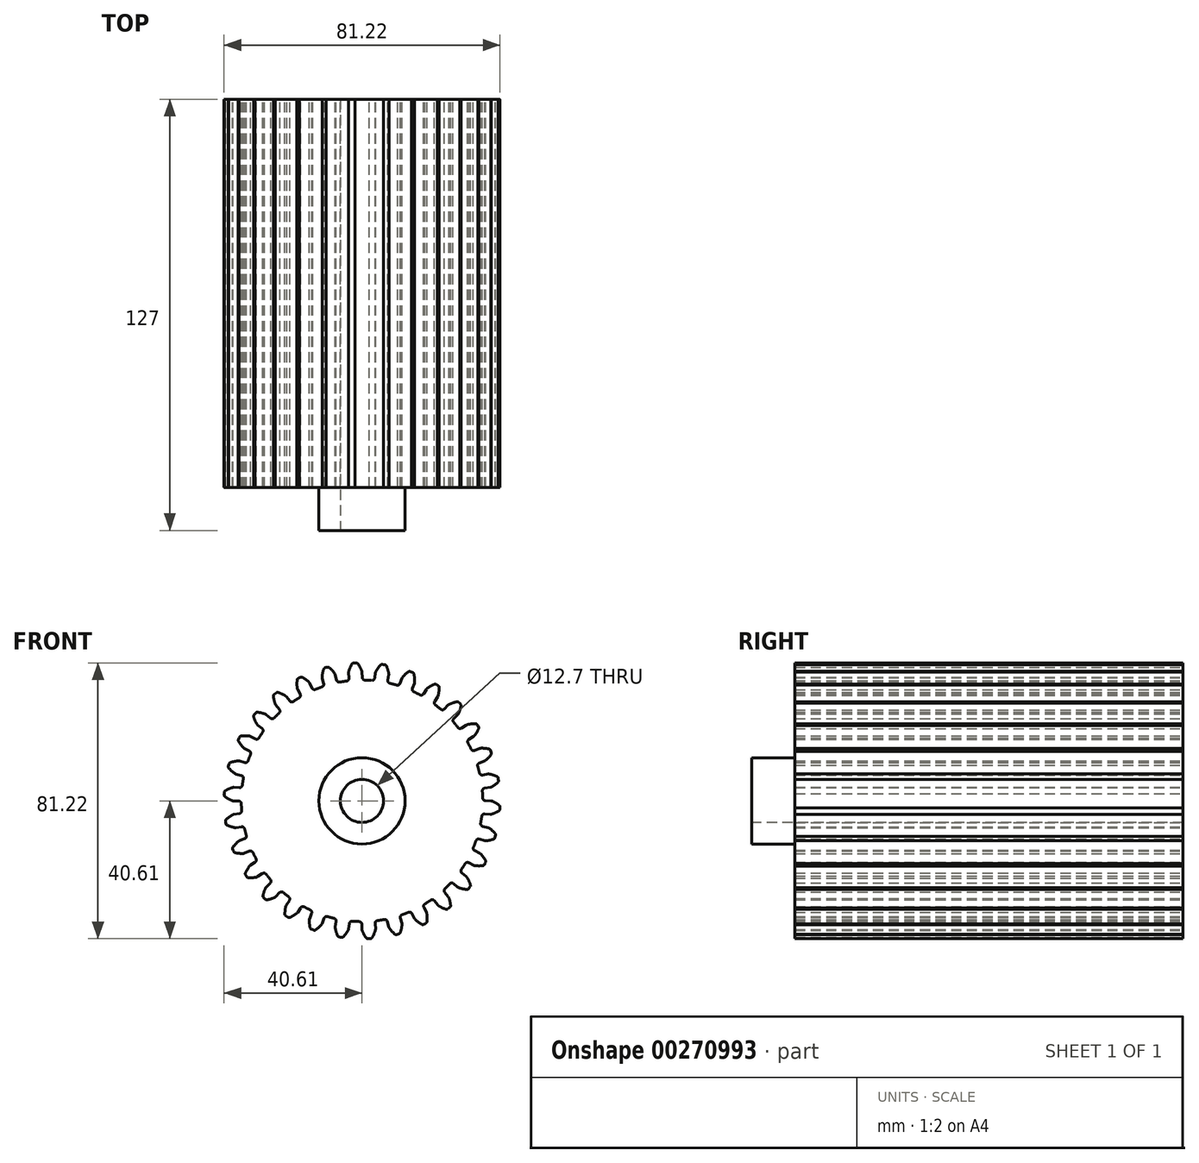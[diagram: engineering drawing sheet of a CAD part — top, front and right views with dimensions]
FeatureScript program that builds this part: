
annotation { "Feature Type Name" : "Feature", "Feature Type Description" : "" }
export const myFeature = defineFeature(function(context is Context, id is Id, definition is map)
    precondition{}
    {
        {
            var Q0;
            Q0=qCreatedBy(makeId("Front.planeOp"),FACE);
            var sketch = newSketch(context, id + "F0", { "sketchPlane" : qUnion([Q0])});
            skArc(sketch, "E0", {"start": v(-4.56, 35.27) * mm, "mid": v(-5.56, 35.12) * mm, "end": v(-6.57, 34.95) * mm});
            skArc(sketch, "E1.trimOffspring", {"start": v(-0.05, 38.23) * mm, "mid": v(-0.6, 39.36) * mm, "end": v(-1.28, 40.4) * mm});
            skLineSegment(sketch, "E2", {"start": v(-1.7, 40.6) * mm, "end": v(-2.13, 40.6) * mm});
            skLineSegment(sketch, "E3", {"start": v(0, 37.97) * mm, "end": v(0.07, 36.31) * mm});
            skLineSegment(sketch, "E4.MirrorCS", {"start": v(-2.55, 40.56) * mm, "end": v(-2.13, 40.6) * mm});
            skArc(sketch, "E5.MirrorCS", {"start": v(-3.95, 38.03) * mm, "mid": v(-3.53, 39.2) * mm, "end": v(-2.95, 40.31) * mm});
            skLineSegment(sketch, "E6.MirrorCS", {"start": v(-3.97, 37.76) * mm, "end": v(-3.86, 36.1) * mm});
            skPoint(sketch, "E7.visualSharp", {"position": v(-2.81, 40.54) * mm});
            skArc(sketch, "E7.filletArc", {"start": v(-2.55, 40.56) * mm, "mid": v(-2.78, 40.49) * mm, "end": v(-2.95, 40.31) * mm});
            skPoint(sketch, "E8.visualSharp", {"position": v(-1.44, 40.61) * mm});
            skArc(sketch, "E8.filletArc", {"start": v(-1.28, 40.4) * mm, "mid": v(-1.46, 40.56) * mm, "end": v(-1.7, 40.6) * mm});
            skPoint(sketch, "E9.visualSharp", {"position": v(-3.82, 35.35) * mm});
            skArc(sketch, "E9.filletArc", {"start": v(-4.56, 35.27) * mm, "mid": v(-4.04, 35.55) * mm, "end": v(-3.86, 36.1) * mm});
            skPoint(sketch, "E10.visualSharp", {"position": v(0.1, 35.56) * mm});
            skArc(sketch, "E10.filletArc", {"start": v(0.07, 36.31) * mm, "mid": v(0.3, 35.78) * mm, "end": v(0.84, 35.55) * mm});
            skPoint(sketch, "E11.visualSharp", {"position": v(0, 38.1) * mm});
            skArc(sketch, "E11.filletArc", {"start": v(0, 37.97) * mm, "mid": v(-0.01, 38.1) * mm, "end": v(-0.05, 38.23) * mm});
            skPoint(sketch, "E12.visualSharp", {"position": v(-3.98, 37.9) * mm});
            skArc(sketch, "E12.filletArc", {"start": v(-3.95, 38.03) * mm, "mid": v(-3.97, 37.9) * mm, "end": v(-3.97, 37.76) * mm});
            skArc(sketch, "E13.1.0", {"start": v(-11.79, 33.55) * mm, "mid": v(-11.35, 33.93) * mm, "end": v(-11.29, 34.51) * mm});
            skLineSegment(sketch, "E13.1.1", {"start": v(-11.74, 36.1) * mm, "end": v(-11.29, 34.51) * mm});
            skArc(sketch, "E13.1.2", {"start": v(-11.77, 36.38) * mm, "mid": v(-11.76, 36.24) * mm, "end": v(-11.74, 36.1) * mm});
            skArc(sketch, "E13.1.3", {"start": v(-11.77, 36.38) * mm, "mid": v(-11.6, 37.61) * mm, "end": v(-11.27, 38.82) * mm});
            skArc(sketch, "E13.1.4", {"start": v(-10.93, 39.14) * mm, "mid": v(-11.14, 39.02) * mm, "end": v(-11.27, 38.82) * mm});
            skLineSegment(sketch, "E13.1.5", {"start": v(-10.1, 39.36) * mm, "end": v(-10.52, 39.26) * mm});
            skArc(sketch, "E13.1.6", {"start": v(-9.65, 39.25) * mm, "mid": v(-9.86, 39.37) * mm, "end": v(-10.1, 39.36) * mm});
            skLineSegment(sketch, "E13.1.7", {"start": v(-10.93, 39.14) * mm, "end": v(-10.52, 39.26) * mm});
            skArc(sketch, "E13.1.8", {"start": v(-8, 37.38) * mm, "mid": v(-8.76, 38.37) * mm, "end": v(-9.65, 39.25) * mm});
            skArc(sketch, "E13.1.9", {"start": v(-7.89, 37.14) * mm, "mid": v(-7.93, 37.27) * mm, "end": v(-8, 37.38) * mm});
            skLineSegment(sketch, "E13.1.10", {"start": v(-7.89, 37.14) * mm, "end": v(-7.48, 35.53) * mm});
            skArc(sketch, "E13.1.11", {"start": v(-7.48, 35.53) * mm, "mid": v(-7.14, 35.06) * mm, "end": v(-6.57, 34.95) * mm});
            skArc(sketch, "E13.2.0", {"start": v(-18.5, 30.37) * mm, "mid": v(-18.15, 30.83) * mm, "end": v(-18.22, 31.41) * mm});
            skLineSegment(sketch, "E13.2.1", {"start": v(-18.99, 32.88) * mm, "end": v(-18.22, 31.41) * mm});
            skArc(sketch, "E13.2.2", {"start": v(-19.07, 33.13) * mm, "mid": v(-19.04, 33) * mm, "end": v(-18.99, 32.88) * mm});
            skArc(sketch, "E13.2.3", {"start": v(-19.07, 33.13) * mm, "mid": v(-19.17, 34.38) * mm, "end": v(-19.1, 35.63) * mm});
            skArc(sketch, "E13.2.4", {"start": v(-18.83, 36.01) * mm, "mid": v(-19.01, 35.85) * mm, "end": v(-19.1, 35.63) * mm});
            skLineSegment(sketch, "E13.2.5", {"start": v(-18.07, 36.4) * mm, "end": v(-18.45, 36.22) * mm});
            skArc(sketch, "E13.2.6", {"start": v(-17.6, 36.4) * mm, "mid": v(-17.83, 36.45) * mm, "end": v(-18.07, 36.4) * mm});
            skLineSegment(sketch, "E13.2.7", {"start": v(-18.83, 36.01) * mm, "end": v(-18.45, 36.22) * mm});
            skArc(sketch, "E13.2.8", {"start": v(-15.6, 34.9) * mm, "mid": v(-16.55, 35.71) * mm, "end": v(-17.6, 36.4) * mm});
            skArc(sketch, "E13.2.9", {"start": v(-15.44, 34.69) * mm, "mid": v(-15.5, 34.8) * mm, "end": v(-15.6, 34.9) * mm});
            skLineSegment(sketch, "E13.2.10", {"start": v(-15.44, 34.69) * mm, "end": v(-14.7, 33.2) * mm});
            skArc(sketch, "E13.2.11", {"start": v(-14.7, 33.2) * mm, "mid": v(-14.27, 32.8) * mm, "end": v(-13.69, 32.82) * mm});
            skArc(sketch, "E13.3.0", {"start": v(-24.41, 25.85) * mm, "mid": v(-24.17, 26.38) * mm, "end": v(-24.35, 26.94) * mm});
            skLineSegment(sketch, "E13.3.1", {"start": v(-25.4, 28.21) * mm, "end": v(-24.35, 26.94) * mm});
            skArc(sketch, "E13.3.2", {"start": v(-25.54, 28.45) * mm, "mid": v(-25.49, 28.32) * mm, "end": v(-25.4, 28.21) * mm});
            skArc(sketch, "E13.3.3", {"start": v(-25.54, 28.45) * mm, "mid": v(-25.9, 29.64) * mm, "end": v(-26.09, 30.88) * mm});
            skArc(sketch, "E13.3.4", {"start": v(-25.9, 31.31) * mm, "mid": v(-26.05, 31.12) * mm, "end": v(-26.09, 30.88) * mm});
            skLineSegment(sketch, "E13.3.5", {"start": v(-25.24, 31.85) * mm, "end": v(-25.58, 31.59) * mm});
            skArc(sketch, "E13.3.6", {"start": v(-24.78, 31.94) * mm, "mid": v(-25.02, 31.95) * mm, "end": v(-25.24, 31.85) * mm});
            skLineSegment(sketch, "E13.3.7", {"start": v(-25.9, 31.31) * mm, "end": v(-25.58, 31.59) * mm});
            skArc(sketch, "E13.3.8", {"start": v(-22.51, 30.9) * mm, "mid": v(-23.61, 31.5) * mm, "end": v(-24.78, 31.94) * mm});
            skArc(sketch, "E13.3.9", {"start": v(-22.31, 30.72) * mm, "mid": v(-22.4, 30.82) * mm, "end": v(-22.51, 30.9) * mm});
            skLineSegment(sketch, "E13.3.10", {"start": v(-22.31, 30.72) * mm, "end": v(-21.29, 29.42) * mm});
            skArc(sketch, "E13.3.11", {"start": v(-21.29, 29.42) * mm, "mid": v(-20.78, 29.12) * mm, "end": v(-20.21, 29.26) * mm});
            skArc(sketch, "E13.4.0", {"start": v(-29.26, 20.21) * mm, "mid": v(-29.12, 20.78) * mm, "end": v(-29.42, 21.29) * mm});
            skLineSegment(sketch, "E13.4.1", {"start": v(-30.72, 22.31) * mm, "end": v(-29.42, 21.29) * mm});
            skArc(sketch, "E13.4.2", {"start": v(-30.9, 22.51) * mm, "mid": v(-30.82, 22.4) * mm, "end": v(-30.72, 22.31) * mm});
            skArc(sketch, "E13.4.3", {"start": v(-30.9, 22.51) * mm, "mid": v(-31.5, 23.61) * mm, "end": v(-31.94, 24.78) * mm});
            skArc(sketch, "E13.4.4", {"start": v(-31.85, 25.24) * mm, "mid": v(-31.95, 25.02) * mm, "end": v(-31.94, 24.78) * mm});
            skLineSegment(sketch, "E13.4.5", {"start": v(-31.31, 25.9) * mm, "end": v(-31.59, 25.58) * mm});
            skArc(sketch, "E13.4.6", {"start": v(-30.88, 26.09) * mm, "mid": v(-31.12, 26.05) * mm, "end": v(-31.31, 25.9) * mm});
            skLineSegment(sketch, "E13.4.7", {"start": v(-31.85, 25.24) * mm, "end": v(-31.59, 25.58) * mm});
            skArc(sketch, "E13.4.8", {"start": v(-28.45, 25.54) * mm, "mid": v(-29.64, 25.9) * mm, "end": v(-30.88, 26.09) * mm});
            skArc(sketch, "E13.4.9", {"start": v(-28.21, 25.4) * mm, "mid": v(-28.32, 25.49) * mm, "end": v(-28.45, 25.54) * mm});
            skLineSegment(sketch, "E13.4.10", {"start": v(-28.21, 25.4) * mm, "end": v(-26.94, 24.35) * mm});
            skArc(sketch, "E13.4.11", {"start": v(-26.94, 24.35) * mm, "mid": v(-26.38, 24.17) * mm, "end": v(-25.85, 24.41) * mm});
            skArc(sketch, "E13.5.0", {"start": v(-32.82, 13.69) * mm, "mid": v(-32.8, 14.27) * mm, "end": v(-33.2, 14.7) * mm});
            skLineSegment(sketch, "E13.5.1", {"start": v(-34.69, 15.44) * mm, "end": v(-33.2, 14.7) * mm});
            skArc(sketch, "E13.5.2", {"start": v(-34.9, 15.6) * mm, "mid": v(-34.8, 15.5) * mm, "end": v(-34.69, 15.44) * mm});
            skArc(sketch, "E13.5.3", {"start": v(-34.9, 15.6) * mm, "mid": v(-35.71, 16.55) * mm, "end": v(-36.4, 17.6) * mm});
            skArc(sketch, "E13.5.4", {"start": v(-36.4, 18.07) * mm, "mid": v(-36.45, 17.83) * mm, "end": v(-36.4, 17.6) * mm});
            skLineSegment(sketch, "E13.5.5", {"start": v(-36.01, 18.83) * mm, "end": v(-36.22, 18.45) * mm});
            skArc(sketch, "E13.5.6", {"start": v(-35.63, 19.1) * mm, "mid": v(-35.85, 19.01) * mm, "end": v(-36.01, 18.83) * mm});
            skLineSegment(sketch, "E13.5.7", {"start": v(-36.4, 18.07) * mm, "end": v(-36.22, 18.45) * mm});
            skArc(sketch, "E13.5.8", {"start": v(-33.13, 19.07) * mm, "mid": v(-34.38, 19.17) * mm, "end": v(-35.63, 19.1) * mm});
            skArc(sketch, "E13.5.9", {"start": v(-32.88, 18.99) * mm, "mid": v(-33, 19.04) * mm, "end": v(-33.13, 19.07) * mm});
            skLineSegment(sketch, "E13.5.10", {"start": v(-32.88, 18.99) * mm, "end": v(-31.41, 18.22) * mm});
            skArc(sketch, "E13.5.11", {"start": v(-31.41, 18.22) * mm, "mid": v(-30.83, 18.15) * mm, "end": v(-30.37, 18.5) * mm});
            skArc(sketch, "E13.6.0", {"start": v(-34.95, 6.57) * mm, "mid": v(-35.06, 7.14) * mm, "end": v(-35.53, 7.48) * mm});
            skLineSegment(sketch, "E13.6.1", {"start": v(-37.14, 7.89) * mm, "end": v(-35.53, 7.48) * mm});
            skArc(sketch, "E13.6.2", {"start": v(-37.38, 8) * mm, "mid": v(-37.27, 7.93) * mm, "end": v(-37.14, 7.89) * mm});
            skArc(sketch, "E13.6.3", {"start": v(-37.38, 8) * mm, "mid": v(-38.37, 8.76) * mm, "end": v(-39.25, 9.65) * mm});
            skArc(sketch, "E13.6.4", {"start": v(-39.36, 10.1) * mm, "mid": v(-39.37, 9.86) * mm, "end": v(-39.25, 9.65) * mm});
            skLineSegment(sketch, "E13.6.5", {"start": v(-39.14, 10.93) * mm, "end": v(-39.26, 10.52) * mm});
            skArc(sketch, "E13.6.6", {"start": v(-38.82, 11.27) * mm, "mid": v(-39.02, 11.14) * mm, "end": v(-39.14, 10.93) * mm});
            skLineSegment(sketch, "E13.6.7", {"start": v(-39.36, 10.1) * mm, "end": v(-39.26, 10.52) * mm});
            skArc(sketch, "E13.6.8", {"start": v(-36.38, 11.77) * mm, "mid": v(-37.61, 11.6) * mm, "end": v(-38.82, 11.27) * mm});
            skArc(sketch, "E13.6.9", {"start": v(-36.1, 11.74) * mm, "mid": v(-36.24, 11.76) * mm, "end": v(-36.38, 11.77) * mm});
            skLineSegment(sketch, "E13.6.10", {"start": v(-36.1, 11.74) * mm, "end": v(-34.51, 11.29) * mm});
            skArc(sketch, "E13.6.11", {"start": v(-34.51, 11.29) * mm, "mid": v(-33.93, 11.35) * mm, "end": v(-33.55, 11.79) * mm});
            skArc(sketch, "E13.7.0", {"start": v(-35.55, -0.84) * mm, "mid": v(-35.78, -0.3) * mm, "end": v(-36.31, -0.07) * mm});
            skLineSegment(sketch, "E13.7.1", {"start": v(-37.97, 0) * mm, "end": v(-36.31, -0.07) * mm});
            skArc(sketch, "E13.7.2", {"start": v(-38.23, 0.05) * mm, "mid": v(-38.1, 0.01) * mm, "end": v(-37.97, 0) * mm});
            skArc(sketch, "E13.7.3", {"start": v(-38.23, 0.05) * mm, "mid": v(-39.36, 0.6) * mm, "end": v(-40.4, 1.28) * mm});
            skArc(sketch, "E13.7.4", {"start": v(-40.6, 1.7) * mm, "mid": v(-40.56, 1.46) * mm, "end": v(-40.4, 1.28) * mm});
            skLineSegment(sketch, "E13.7.5", {"start": v(-40.56, 2.55) * mm, "end": v(-40.6, 2.13) * mm});
            skArc(sketch, "E13.7.6", {"start": v(-40.31, 2.95) * mm, "mid": v(-40.49, 2.78) * mm, "end": v(-40.56, 2.55) * mm});
            skLineSegment(sketch, "E13.7.7", {"start": v(-40.6, 1.7) * mm, "end": v(-40.6, 2.13) * mm});
            skArc(sketch, "E13.7.8", {"start": v(-38.03, 3.95) * mm, "mid": v(-39.2, 3.53) * mm, "end": v(-40.31, 2.95) * mm});
            skArc(sketch, "E13.7.9", {"start": v(-37.76, 3.97) * mm, "mid": v(-37.9, 3.97) * mm, "end": v(-38.03, 3.95) * mm});
            skLineSegment(sketch, "E13.7.10", {"start": v(-37.76, 3.97) * mm, "end": v(-36.1, 3.86) * mm});
            skArc(sketch, "E13.7.11", {"start": v(-36.1, 3.86) * mm, "mid": v(-35.55, 4.04) * mm, "end": v(-35.27, 4.56) * mm});
            skArc(sketch, "E13.8.0", {"start": v(-34.6, -8.22) * mm, "mid": v(-34.93, -7.74) * mm, "end": v(-35.5, -7.62) * mm});
            skLineSegment(sketch, "E13.8.1", {"start": v(-37.13, -7.9) * mm, "end": v(-35.5, -7.62) * mm});
            skArc(sketch, "E13.8.2", {"start": v(-37.4, -7.9) * mm, "mid": v(-37.27, -7.91) * mm, "end": v(-37.13, -7.9) * mm});
            skArc(sketch, "E13.8.3", {"start": v(-37.4, -7.9) * mm, "mid": v(-38.62, -7.6) * mm, "end": v(-39.79, -7.15) * mm});
            skArc(sketch, "E13.8.4", {"start": v(-40.07, -6.78) * mm, "mid": v(-39.97, -7) * mm, "end": v(-39.79, -7.15) * mm});
            skLineSegment(sketch, "E13.8.5", {"start": v(-40.2, -5.93) * mm, "end": v(-40.15, -6.36) * mm});
            skArc(sketch, "E13.8.6", {"start": v(-40.05, -5.5) * mm, "mid": v(-40.18, -5.7) * mm, "end": v(-40.2, -5.93) * mm});
            skLineSegment(sketch, "E13.8.7", {"start": v(-40.07, -6.78) * mm, "end": v(-40.15, -6.36) * mm});
            skArc(sketch, "E13.8.8", {"start": v(-38.02, -4.05) * mm, "mid": v(-39.08, -4.7) * mm, "end": v(-40.05, -5.5) * mm});
            skArc(sketch, "E13.8.9", {"start": v(-37.76, -3.96) * mm, "mid": v(-37.9, -4) * mm, "end": v(-38.02, -4.05) * mm});
            skLineSegment(sketch, "E13.8.10", {"start": v(-37.76, -3.96) * mm, "end": v(-36.12, -3.73) * mm});
            skArc(sketch, "E13.8.11", {"start": v(-36.12, -3.73) * mm, "mid": v(-35.61, -3.44) * mm, "end": v(-35.44, -2.88) * mm});
            skArc(sketch, "E13.9.0", {"start": v(-32.13, -15.23) * mm, "mid": v(-32.56, -14.83) * mm, "end": v(-33.14, -14.83) * mm});
            skLineSegment(sketch, "E13.9.1", {"start": v(-34.68, -15.45) * mm, "end": v(-33.14, -14.83) * mm});
            skArc(sketch, "E13.9.2", {"start": v(-34.95, -15.5) * mm, "mid": v(-34.81, -15.49) * mm, "end": v(-34.68, -15.45) * mm});
            skArc(sketch, "E13.9.3", {"start": v(-34.95, -15.5) * mm, "mid": v(-36.2, -15.47) * mm, "end": v(-37.43, -15.27) * mm});
            skArc(sketch, "E13.9.4", {"start": v(-37.79, -14.96) * mm, "mid": v(-37.64, -15.16) * mm, "end": v(-37.43, -15.27) * mm});
            skLineSegment(sketch, "E13.9.5", {"start": v(-38.1, -14.16) * mm, "end": v(-37.95, -14.57) * mm});
            skArc(sketch, "E13.9.6", {"start": v(-38.03, -13.7) * mm, "mid": v(-38.12, -13.92) * mm, "end": v(-38.1, -14.16) * mm});
            skLineSegment(sketch, "E13.9.7", {"start": v(-37.79, -14.96) * mm, "end": v(-37.95, -14.57) * mm});
            skArc(sketch, "E13.9.8", {"start": v(-36.34, -11.86) * mm, "mid": v(-37.25, -12.72) * mm, "end": v(-38.03, -13.7) * mm});
            skArc(sketch, "E13.9.9", {"start": v(-36.1, -11.73) * mm, "mid": v(-36.23, -11.78) * mm, "end": v(-36.34, -11.86) * mm});
            skLineSegment(sketch, "E13.9.10", {"start": v(-36.1, -11.73) * mm, "end": v(-34.56, -11.16) * mm});
            skArc(sketch, "E13.9.11", {"start": v(-34.56, -11.16) * mm, "mid": v(-34.12, -10.77) * mm, "end": v(-34.07, -10.18) * mm});
            skArc(sketch, "E13.10.0", {"start": v(-28.26, -21.58) * mm, "mid": v(-28.77, -21.28) * mm, "end": v(-29.34, -21.4) * mm});
            skLineSegment(sketch, "E13.10.1", {"start": v(-30.71, -22.32) * mm, "end": v(-29.34, -21.4) * mm});
            skArc(sketch, "E13.10.2", {"start": v(-30.96, -22.43) * mm, "mid": v(-30.83, -22.39) * mm, "end": v(-30.71, -22.32) * mm});
            skArc(sketch, "E13.10.3", {"start": v(-30.96, -22.43) * mm, "mid": v(-32.19, -22.65) * mm, "end": v(-33.44, -22.72) * mm});
            skArc(sketch, "E13.10.4", {"start": v(-33.85, -22.5) * mm, "mid": v(-33.67, -22.66) * mm, "end": v(-33.44, -22.72) * mm});
            skLineSegment(sketch, "E13.10.5", {"start": v(-34.32, -21.77) * mm, "end": v(-34.09, -22.14) * mm});
            skArc(sketch, "E13.10.6", {"start": v(-34.35, -21.3) * mm, "mid": v(-34.4, -21.54) * mm, "end": v(-34.32, -21.77) * mm});
            skLineSegment(sketch, "E13.10.7", {"start": v(-33.85, -22.5) * mm, "end": v(-34.09, -22.14) * mm});
            skArc(sketch, "E13.10.8", {"start": v(-33.08, -19.16) * mm, "mid": v(-33.79, -20.2) * mm, "end": v(-34.35, -21.3) * mm});
            skArc(sketch, "E13.10.9", {"start": v(-32.88, -18.98) * mm, "mid": v(-33, -19.06) * mm, "end": v(-33.08, -19.16) * mm});
            skLineSegment(sketch, "E13.10.10", {"start": v(-32.88, -18.98) * mm, "end": v(-31.48, -18.1) * mm});
            skArc(sketch, "E13.10.11", {"start": v(-31.48, -18.1) * mm, "mid": v(-31.14, -17.62) * mm, "end": v(-31.2, -17.04) * mm});
            skArc(sketch, "E13.11.0", {"start": v(-23.16, -26.98) * mm, "mid": v(-23.71, -26.8) * mm, "end": v(-24.25, -27.03) * mm});
            skLineSegment(sketch, "E13.11.1", {"start": v(-25.4, -28.22) * mm, "end": v(-24.25, -27.03) * mm});
            skArc(sketch, "E13.11.2", {"start": v(-25.62, -28.38) * mm, "mid": v(-25.5, -28.3) * mm, "end": v(-25.4, -28.22) * mm});
            skArc(sketch, "E13.11.3", {"start": v(-25.62, -28.38) * mm, "mid": v(-26.77, -28.85) * mm, "end": v(-27.98, -29.17) * mm});
            skArc(sketch, "E13.11.4", {"start": v(-28.43, -29.04) * mm, "mid": v(-28.22, -29.16) * mm, "end": v(-27.98, -29.17) * mm});
            skLineSegment(sketch, "E13.11.5", {"start": v(-29.04, -28.43) * mm, "end": v(-28.74, -28.74) * mm});
            skArc(sketch, "E13.11.6", {"start": v(-29.17, -27.98) * mm, "mid": v(-29.16, -28.22) * mm, "end": v(-29.04, -28.43) * mm});
            skLineSegment(sketch, "E13.11.7", {"start": v(-28.43, -29.04) * mm, "end": v(-28.74, -28.74) * mm});
            skArc(sketch, "E13.11.8", {"start": v(-28.38, -25.62) * mm, "mid": v(-28.85, -26.77) * mm, "end": v(-29.17, -27.98) * mm});
            skArc(sketch, "E13.11.9", {"start": v(-28.22, -25.4) * mm, "mid": v(-28.3, -25.5) * mm, "end": v(-28.38, -25.62) * mm});
            skLineSegment(sketch, "E13.11.10", {"start": v(-28.22, -25.4) * mm, "end": v(-27.03, -24.25) * mm});
            skArc(sketch, "E13.11.11", {"start": v(-27.03, -24.25) * mm, "mid": v(-26.8, -23.71) * mm, "end": v(-26.98, -23.16) * mm});
            skArc(sketch, "E13.12.0", {"start": v(-17.04, -31.2) * mm, "mid": v(-17.62, -31.14) * mm, "end": v(-18.1, -31.48) * mm});
            skLineSegment(sketch, "E13.12.1", {"start": v(-18.98, -32.88) * mm, "end": v(-18.1, -31.48) * mm});
            skArc(sketch, "E13.12.2", {"start": v(-19.16, -33.08) * mm, "mid": v(-19.06, -33) * mm, "end": v(-18.98, -32.88) * mm});
            skArc(sketch, "E13.12.3", {"start": v(-19.16, -33.08) * mm, "mid": v(-20.2, -33.79) * mm, "end": v(-21.3, -34.35) * mm});
            skArc(sketch, "E13.12.4", {"start": v(-21.77, -34.32) * mm, "mid": v(-21.54, -34.4) * mm, "end": v(-21.3, -34.35) * mm});
            skLineSegment(sketch, "E13.12.5", {"start": v(-22.5, -33.85) * mm, "end": v(-22.14, -34.09) * mm});
            skArc(sketch, "E13.12.6", {"start": v(-22.72, -33.44) * mm, "mid": v(-22.66, -33.67) * mm, "end": v(-22.5, -33.85) * mm});
            skLineSegment(sketch, "E13.12.7", {"start": v(-21.77, -34.32) * mm, "end": v(-22.14, -34.09) * mm});
            skArc(sketch, "E13.12.8", {"start": v(-22.43, -30.96) * mm, "mid": v(-22.65, -32.19) * mm, "end": v(-22.72, -33.44) * mm});
            skArc(sketch, "E13.12.9", {"start": v(-22.32, -30.71) * mm, "mid": v(-22.39, -30.83) * mm, "end": v(-22.43, -30.96) * mm});
            skLineSegment(sketch, "E13.12.10", {"start": v(-22.32, -30.71) * mm, "end": v(-21.4, -29.34) * mm});
            skArc(sketch, "E13.12.11", {"start": v(-21.4, -29.34) * mm, "mid": v(-21.28, -28.77) * mm, "end": v(-21.58, -28.26) * mm});
            skArc(sketch, "E13.13.0", {"start": v(-10.18, -34.07) * mm, "mid": v(-10.77, -34.12) * mm, "end": v(-11.16, -34.56) * mm});
            skLineSegment(sketch, "E13.13.1", {"start": v(-11.73, -36.1) * mm, "end": v(-11.16, -34.56) * mm});
            skArc(sketch, "E13.13.2", {"start": v(-11.86, -36.34) * mm, "mid": v(-11.78, -36.23) * mm, "end": v(-11.73, -36.1) * mm});
            skArc(sketch, "E13.13.3", {"start": v(-11.86, -36.34) * mm, "mid": v(-12.72, -37.25) * mm, "end": v(-13.7, -38.03) * mm});
            skArc(sketch, "E13.13.4", {"start": v(-14.16, -38.1) * mm, "mid": v(-13.92, -38.12) * mm, "end": v(-13.7, -38.03) * mm});
            skLineSegment(sketch, "E13.13.5", {"start": v(-14.96, -37.79) * mm, "end": v(-14.57, -37.95) * mm});
            skArc(sketch, "E13.13.6", {"start": v(-15.27, -37.43) * mm, "mid": v(-15.16, -37.64) * mm, "end": v(-14.96, -37.79) * mm});
            skLineSegment(sketch, "E13.13.7", {"start": v(-14.16, -38.1) * mm, "end": v(-14.57, -37.95) * mm});
            skArc(sketch, "E13.13.8", {"start": v(-15.5, -34.95) * mm, "mid": v(-15.47, -36.2) * mm, "end": v(-15.27, -37.43) * mm});
            skArc(sketch, "E13.13.9", {"start": v(-15.45, -34.68) * mm, "mid": v(-15.49, -34.81) * mm, "end": v(-15.5, -34.95) * mm});
            skLineSegment(sketch, "E13.13.10", {"start": v(-15.45, -34.68) * mm, "end": v(-14.83, -33.14) * mm});
            skArc(sketch, "E13.13.11", {"start": v(-14.83, -33.14) * mm, "mid": v(-14.83, -32.56) * mm, "end": v(-15.23, -32.13) * mm});
            skArc(sketch, "E13.14.0", {"start": v(-2.88, -35.44) * mm, "mid": v(-3.44, -35.61) * mm, "end": v(-3.73, -36.12) * mm});
            skLineSegment(sketch, "E13.14.1", {"start": v(-3.96, -37.76) * mm, "end": v(-3.73, -36.12) * mm});
            skArc(sketch, "E13.14.2", {"start": v(-4.05, -38.02) * mm, "mid": v(-4, -37.9) * mm, "end": v(-3.96, -37.76) * mm});
            skArc(sketch, "E13.14.3", {"start": v(-4.05, -38.02) * mm, "mid": v(-4.7, -39.08) * mm, "end": v(-5.5, -40.05) * mm});
            skArc(sketch, "E13.14.4", {"start": v(-5.93, -40.2) * mm, "mid": v(-5.7, -40.18) * mm, "end": v(-5.5, -40.05) * mm});
            skLineSegment(sketch, "E13.14.5", {"start": v(-6.78, -40.07) * mm, "end": v(-6.36, -40.15) * mm});
            skArc(sketch, "E13.14.6", {"start": v(-7.15, -39.79) * mm, "mid": v(-7, -39.97) * mm, "end": v(-6.78, -40.07) * mm});
            skLineSegment(sketch, "E13.14.7", {"start": v(-5.93, -40.2) * mm, "end": v(-6.36, -40.15) * mm});
            skArc(sketch, "E13.14.8", {"start": v(-7.9, -37.4) * mm, "mid": v(-7.6, -38.62) * mm, "end": v(-7.15, -39.79) * mm});
            skArc(sketch, "E13.14.9", {"start": v(-7.9, -37.13) * mm, "mid": v(-7.91, -37.27) * mm, "end": v(-7.9, -37.4) * mm});
            skLineSegment(sketch, "E13.14.10", {"start": v(-7.9, -37.13) * mm, "end": v(-7.62, -35.5) * mm});
            skArc(sketch, "E13.14.11", {"start": v(-7.62, -35.5) * mm, "mid": v(-7.74, -34.93) * mm, "end": v(-8.22, -34.6) * mm});
            skArc(sketch, "E13.15.0", {"start": v(4.56, -35.27) * mm, "mid": v(4.04, -35.55) * mm, "end": v(3.86, -36.1) * mm});
            skLineSegment(sketch, "E13.15.1", {"start": v(3.97, -37.76) * mm, "end": v(3.86, -36.1) * mm});
            skArc(sketch, "E13.15.2", {"start": v(3.95, -38.03) * mm, "mid": v(3.97, -37.9) * mm, "end": v(3.97, -37.76) * mm});
            skArc(sketch, "E13.15.3", {"start": v(3.95, -38.03) * mm, "mid": v(3.53, -39.2) * mm, "end": v(2.95, -40.31) * mm});
            skArc(sketch, "E13.15.4", {"start": v(2.55, -40.56) * mm, "mid": v(2.78, -40.49) * mm, "end": v(2.95, -40.31) * mm});
            skLineSegment(sketch, "E13.15.5", {"start": v(1.7, -40.6) * mm, "end": v(2.13, -40.6) * mm});
            skArc(sketch, "E13.15.6", {"start": v(1.28, -40.4) * mm, "mid": v(1.46, -40.56) * mm, "end": v(1.7, -40.6) * mm});
            skLineSegment(sketch, "E13.15.7", {"start": v(2.55, -40.56) * mm, "end": v(2.13, -40.6) * mm});
            skArc(sketch, "E13.15.8", {"start": v(0.05, -38.23) * mm, "mid": v(0.6, -39.36) * mm, "end": v(1.28, -40.4) * mm});
            skArc(sketch, "E13.15.9", {"start": v(0, -37.97) * mm, "mid": v(0.01, -38.1) * mm, "end": v(0.05, -38.23) * mm});
            skLineSegment(sketch, "E13.15.10", {"start": v(0, -37.97) * mm, "end": v(-0.07, -36.31) * mm});
            skArc(sketch, "E13.15.11", {"start": v(-0.07, -36.31) * mm, "mid": v(-0.3, -35.78) * mm, "end": v(-0.84, -35.55) * mm});
            skArc(sketch, "E13.16.0", {"start": v(11.79, -33.55) * mm, "mid": v(11.35, -33.93) * mm, "end": v(11.29, -34.51) * mm});
            skLineSegment(sketch, "E13.16.1", {"start": v(11.74, -36.1) * mm, "end": v(11.29, -34.51) * mm});
            skArc(sketch, "E13.16.2", {"start": v(11.77, -36.38) * mm, "mid": v(11.76, -36.24) * mm, "end": v(11.74, -36.1) * mm});
            skArc(sketch, "E13.16.3", {"start": v(11.77, -36.38) * mm, "mid": v(11.6, -37.61) * mm, "end": v(11.27, -38.82) * mm});
            skArc(sketch, "E13.16.4", {"start": v(10.93, -39.14) * mm, "mid": v(11.14, -39.02) * mm, "end": v(11.27, -38.82) * mm});
            skLineSegment(sketch, "E13.16.5", {"start": v(10.1, -39.36) * mm, "end": v(10.52, -39.26) * mm});
            skArc(sketch, "E13.16.6", {"start": v(9.65, -39.25) * mm, "mid": v(9.86, -39.37) * mm, "end": v(10.1, -39.36) * mm});
            skLineSegment(sketch, "E13.16.7", {"start": v(10.93, -39.14) * mm, "end": v(10.52, -39.26) * mm});
            skArc(sketch, "E13.16.8", {"start": v(8, -37.38) * mm, "mid": v(8.76, -38.37) * mm, "end": v(9.65, -39.25) * mm});
            skArc(sketch, "E13.16.9", {"start": v(7.89, -37.14) * mm, "mid": v(7.93, -37.27) * mm, "end": v(8, -37.38) * mm});
            skLineSegment(sketch, "E13.16.10", {"start": v(7.89, -37.14) * mm, "end": v(7.48, -35.53) * mm});
            skArc(sketch, "E13.16.11", {"start": v(7.48, -35.53) * mm, "mid": v(7.14, -35.06) * mm, "end": v(6.57, -34.95) * mm});
            skArc(sketch, "E13.17.0", {"start": v(18.5, -30.37) * mm, "mid": v(18.15, -30.83) * mm, "end": v(18.22, -31.41) * mm});
            skLineSegment(sketch, "E13.17.1", {"start": v(18.99, -32.88) * mm, "end": v(18.22, -31.41) * mm});
            skArc(sketch, "E13.17.2", {"start": v(19.07, -33.13) * mm, "mid": v(19.04, -33) * mm, "end": v(18.99, -32.88) * mm});
            skArc(sketch, "E13.17.3", {"start": v(19.07, -33.13) * mm, "mid": v(19.17, -34.38) * mm, "end": v(19.1, -35.63) * mm});
            skArc(sketch, "E13.17.4", {"start": v(18.83, -36.01) * mm, "mid": v(19.01, -35.85) * mm, "end": v(19.1, -35.63) * mm});
            skLineSegment(sketch, "E13.17.5", {"start": v(18.07, -36.4) * mm, "end": v(18.45, -36.22) * mm});
            skArc(sketch, "E13.17.6", {"start": v(17.6, -36.4) * mm, "mid": v(17.83, -36.45) * mm, "end": v(18.07, -36.4) * mm});
            skLineSegment(sketch, "E13.17.7", {"start": v(18.83, -36.01) * mm, "end": v(18.45, -36.22) * mm});
            skArc(sketch, "E13.17.8", {"start": v(15.6, -34.9) * mm, "mid": v(16.55, -35.71) * mm, "end": v(17.6, -36.4) * mm});
            skArc(sketch, "E13.17.9", {"start": v(15.44, -34.69) * mm, "mid": v(15.5, -34.8) * mm, "end": v(15.6, -34.9) * mm});
            skLineSegment(sketch, "E13.17.10", {"start": v(15.44, -34.69) * mm, "end": v(14.7, -33.2) * mm});
            skArc(sketch, "E13.17.11", {"start": v(14.7, -33.2) * mm, "mid": v(14.27, -32.8) * mm, "end": v(13.69, -32.82) * mm});
            skArc(sketch, "E13.18.0", {"start": v(24.41, -25.85) * mm, "mid": v(24.17, -26.38) * mm, "end": v(24.35, -26.94) * mm});
            skLineSegment(sketch, "E13.18.1", {"start": v(25.4, -28.21) * mm, "end": v(24.35, -26.94) * mm});
            skArc(sketch, "E13.18.2", {"start": v(25.54, -28.45) * mm, "mid": v(25.49, -28.32) * mm, "end": v(25.4, -28.21) * mm});
            skArc(sketch, "E13.18.3", {"start": v(25.54, -28.45) * mm, "mid": v(25.9, -29.64) * mm, "end": v(26.09, -30.88) * mm});
            skArc(sketch, "E13.18.4", {"start": v(25.9, -31.31) * mm, "mid": v(26.05, -31.12) * mm, "end": v(26.09, -30.88) * mm});
            skLineSegment(sketch, "E13.18.5", {"start": v(25.24, -31.85) * mm, "end": v(25.58, -31.59) * mm});
            skArc(sketch, "E13.18.6", {"start": v(24.78, -31.94) * mm, "mid": v(25.02, -31.95) * mm, "end": v(25.24, -31.85) * mm});
            skLineSegment(sketch, "E13.18.7", {"start": v(25.9, -31.31) * mm, "end": v(25.58, -31.59) * mm});
            skArc(sketch, "E13.18.8", {"start": v(22.51, -30.9) * mm, "mid": v(23.61, -31.5) * mm, "end": v(24.78, -31.94) * mm});
            skArc(sketch, "E13.18.9", {"start": v(22.31, -30.72) * mm, "mid": v(22.4, -30.82) * mm, "end": v(22.51, -30.9) * mm});
            skLineSegment(sketch, "E13.18.10", {"start": v(22.31, -30.72) * mm, "end": v(21.29, -29.42) * mm});
            skArc(sketch, "E13.18.11", {"start": v(21.29, -29.42) * mm, "mid": v(20.78, -29.12) * mm, "end": v(20.21, -29.26) * mm});
            skArc(sketch, "E13.19.0", {"start": v(29.26, -20.21) * mm, "mid": v(29.12, -20.78) * mm, "end": v(29.42, -21.29) * mm});
            skLineSegment(sketch, "E13.19.1", {"start": v(30.72, -22.31) * mm, "end": v(29.42, -21.29) * mm});
            skArc(sketch, "E13.19.2", {"start": v(30.9, -22.51) * mm, "mid": v(30.82, -22.4) * mm, "end": v(30.72, -22.31) * mm});
            skArc(sketch, "E13.19.3", {"start": v(30.9, -22.51) * mm, "mid": v(31.5, -23.61) * mm, "end": v(31.94, -24.78) * mm});
            skArc(sketch, "E13.19.4", {"start": v(31.85, -25.24) * mm, "mid": v(31.95, -25.02) * mm, "end": v(31.94, -24.78) * mm});
            skLineSegment(sketch, "E13.19.5", {"start": v(31.31, -25.9) * mm, "end": v(31.59, -25.58) * mm});
            skArc(sketch, "E13.19.6", {"start": v(30.88, -26.09) * mm, "mid": v(31.12, -26.05) * mm, "end": v(31.31, -25.9) * mm});
            skLineSegment(sketch, "E13.19.7", {"start": v(31.85, -25.24) * mm, "end": v(31.59, -25.58) * mm});
            skArc(sketch, "E13.19.8", {"start": v(28.45, -25.54) * mm, "mid": v(29.64, -25.9) * mm, "end": v(30.88, -26.09) * mm});
            skArc(sketch, "E13.19.9", {"start": v(28.21, -25.4) * mm, "mid": v(28.32, -25.49) * mm, "end": v(28.45, -25.54) * mm});
            skLineSegment(sketch, "E13.19.10", {"start": v(28.21, -25.4) * mm, "end": v(26.94, -24.35) * mm});
            skArc(sketch, "E13.19.11", {"start": v(26.94, -24.35) * mm, "mid": v(26.38, -24.17) * mm, "end": v(25.85, -24.41) * mm});
            skArc(sketch, "E13.20.0", {"start": v(32.82, -13.69) * mm, "mid": v(32.8, -14.27) * mm, "end": v(33.2, -14.7) * mm});
            skLineSegment(sketch, "E13.20.1", {"start": v(34.69, -15.44) * mm, "end": v(33.2, -14.7) * mm});
            skArc(sketch, "E13.20.2", {"start": v(34.9, -15.6) * mm, "mid": v(34.8, -15.5) * mm, "end": v(34.69, -15.44) * mm});
            skArc(sketch, "E13.20.3", {"start": v(34.9, -15.6) * mm, "mid": v(35.71, -16.55) * mm, "end": v(36.4, -17.6) * mm});
            skArc(sketch, "E13.20.4", {"start": v(36.4, -18.07) * mm, "mid": v(36.45, -17.83) * mm, "end": v(36.4, -17.6) * mm});
            skLineSegment(sketch, "E13.20.5", {"start": v(36.01, -18.83) * mm, "end": v(36.22, -18.45) * mm});
            skArc(sketch, "E13.20.6", {"start": v(35.63, -19.1) * mm, "mid": v(35.85, -19.01) * mm, "end": v(36.01, -18.83) * mm});
            skLineSegment(sketch, "E13.20.7", {"start": v(36.4, -18.07) * mm, "end": v(36.22, -18.45) * mm});
            skArc(sketch, "E13.20.8", {"start": v(33.13, -19.07) * mm, "mid": v(34.38, -19.17) * mm, "end": v(35.63, -19.1) * mm});
            skArc(sketch, "E13.20.9", {"start": v(32.88, -18.99) * mm, "mid": v(33, -19.04) * mm, "end": v(33.13, -19.07) * mm});
            skLineSegment(sketch, "E13.20.10", {"start": v(32.88, -18.99) * mm, "end": v(31.41, -18.22) * mm});
            skArc(sketch, "E13.20.11", {"start": v(31.41, -18.22) * mm, "mid": v(30.83, -18.15) * mm, "end": v(30.37, -18.5) * mm});
            skArc(sketch, "E13.21.0", {"start": v(34.95, -6.57) * mm, "mid": v(35.06, -7.14) * mm, "end": v(35.53, -7.48) * mm});
            skLineSegment(sketch, "E13.21.1", {"start": v(37.14, -7.89) * mm, "end": v(35.53, -7.48) * mm});
            skArc(sketch, "E13.21.2", {"start": v(37.38, -8) * mm, "mid": v(37.27, -7.93) * mm, "end": v(37.14, -7.89) * mm});
            skArc(sketch, "E13.21.3", {"start": v(37.38, -8) * mm, "mid": v(38.37, -8.76) * mm, "end": v(39.25, -9.65) * mm});
            skArc(sketch, "E13.21.4", {"start": v(39.36, -10.1) * mm, "mid": v(39.37, -9.86) * mm, "end": v(39.25, -9.65) * mm});
            skLineSegment(sketch, "E13.21.5", {"start": v(39.14, -10.93) * mm, "end": v(39.26, -10.52) * mm});
            skArc(sketch, "E13.21.6", {"start": v(38.82, -11.27) * mm, "mid": v(39.02, -11.14) * mm, "end": v(39.14, -10.93) * mm});
            skLineSegment(sketch, "E13.21.7", {"start": v(39.36, -10.1) * mm, "end": v(39.26, -10.52) * mm});
            skArc(sketch, "E13.21.8", {"start": v(36.38, -11.77) * mm, "mid": v(37.61, -11.6) * mm, "end": v(38.82, -11.27) * mm});
            skArc(sketch, "E13.21.9", {"start": v(36.1, -11.74) * mm, "mid": v(36.24, -11.76) * mm, "end": v(36.38, -11.77) * mm});
            skLineSegment(sketch, "E13.21.10", {"start": v(36.1, -11.74) * mm, "end": v(34.51, -11.29) * mm});
            skArc(sketch, "E13.21.11", {"start": v(34.51, -11.29) * mm, "mid": v(33.93, -11.35) * mm, "end": v(33.55, -11.79) * mm});
            skArc(sketch, "E13.22.0", {"start": v(35.55, 0.84) * mm, "mid": v(35.78, 0.3) * mm, "end": v(36.31, 0.07) * mm});
            skLineSegment(sketch, "E13.22.1", {"start": v(37.97, 0) * mm, "end": v(36.31, 0.07) * mm});
            skArc(sketch, "E13.22.2", {"start": v(38.23, -0.05) * mm, "mid": v(38.1, -0.01) * mm, "end": v(37.97, 0) * mm});
            skArc(sketch, "E13.22.3", {"start": v(38.23, -0.05) * mm, "mid": v(39.36, -0.6) * mm, "end": v(40.4, -1.28) * mm});
            skArc(sketch, "E13.22.4", {"start": v(40.6, -1.7) * mm, "mid": v(40.56, -1.46) * mm, "end": v(40.4, -1.28) * mm});
            skLineSegment(sketch, "E13.22.5", {"start": v(40.56, -2.55) * mm, "end": v(40.6, -2.13) * mm});
            skArc(sketch, "E13.22.6", {"start": v(40.31, -2.95) * mm, "mid": v(40.49, -2.78) * mm, "end": v(40.56, -2.55) * mm});
            skLineSegment(sketch, "E13.22.7", {"start": v(40.6, -1.7) * mm, "end": v(40.6, -2.13) * mm});
            skArc(sketch, "E13.22.8", {"start": v(38.03, -3.95) * mm, "mid": v(39.2, -3.53) * mm, "end": v(40.31, -2.95) * mm});
            skArc(sketch, "E13.22.9", {"start": v(37.76, -3.97) * mm, "mid": v(37.9, -3.97) * mm, "end": v(38.03, -3.95) * mm});
            skLineSegment(sketch, "E13.22.10", {"start": v(37.76, -3.97) * mm, "end": v(36.1, -3.86) * mm});
            skArc(sketch, "E13.22.11", {"start": v(36.1, -3.86) * mm, "mid": v(35.55, -4.04) * mm, "end": v(35.27, -4.56) * mm});
            skArc(sketch, "E13.23.0", {"start": v(34.6, 8.22) * mm, "mid": v(34.93, 7.74) * mm, "end": v(35.5, 7.62) * mm});
            skLineSegment(sketch, "E13.23.1", {"start": v(37.13, 7.9) * mm, "end": v(35.5, 7.62) * mm});
            skArc(sketch, "E13.23.2", {"start": v(37.4, 7.9) * mm, "mid": v(37.27, 7.91) * mm, "end": v(37.13, 7.9) * mm});
            skArc(sketch, "E13.23.3", {"start": v(37.4, 7.9) * mm, "mid": v(38.62, 7.6) * mm, "end": v(39.79, 7.15) * mm});
            skArc(sketch, "E13.23.4", {"start": v(40.07, 6.78) * mm, "mid": v(39.97, 7) * mm, "end": v(39.79, 7.15) * mm});
            skLineSegment(sketch, "E13.23.5", {"start": v(40.2, 5.93) * mm, "end": v(40.15, 6.36) * mm});
            skArc(sketch, "E13.23.6", {"start": v(40.05, 5.5) * mm, "mid": v(40.18, 5.7) * mm, "end": v(40.2, 5.93) * mm});
            skLineSegment(sketch, "E13.23.7", {"start": v(40.07, 6.78) * mm, "end": v(40.15, 6.36) * mm});
            skArc(sketch, "E13.23.8", {"start": v(38.02, 4.05) * mm, "mid": v(39.08, 4.7) * mm, "end": v(40.05, 5.5) * mm});
            skArc(sketch, "E13.23.9", {"start": v(37.76, 3.96) * mm, "mid": v(37.9, 4) * mm, "end": v(38.02, 4.05) * mm});
            skLineSegment(sketch, "E13.23.10", {"start": v(37.76, 3.96) * mm, "end": v(36.12, 3.73) * mm});
            skArc(sketch, "E13.23.11", {"start": v(36.12, 3.73) * mm, "mid": v(35.61, 3.44) * mm, "end": v(35.44, 2.88) * mm});
            skArc(sketch, "E13.24.0", {"start": v(32.13, 15.23) * mm, "mid": v(32.56, 14.83) * mm, "end": v(33.14, 14.83) * mm});
            skLineSegment(sketch, "E13.24.1", {"start": v(34.68, 15.45) * mm, "end": v(33.14, 14.83) * mm});
            skArc(sketch, "E13.24.2", {"start": v(34.95, 15.5) * mm, "mid": v(34.81, 15.49) * mm, "end": v(34.68, 15.45) * mm});
            skArc(sketch, "E13.24.3", {"start": v(34.95, 15.5) * mm, "mid": v(36.2, 15.47) * mm, "end": v(37.43, 15.27) * mm});
            skArc(sketch, "E13.24.4", {"start": v(37.79, 14.96) * mm, "mid": v(37.64, 15.16) * mm, "end": v(37.43, 15.27) * mm});
            skLineSegment(sketch, "E13.24.5", {"start": v(38.1, 14.16) * mm, "end": v(37.95, 14.57) * mm});
            skArc(sketch, "E13.24.6", {"start": v(38.03, 13.7) * mm, "mid": v(38.12, 13.92) * mm, "end": v(38.1, 14.16) * mm});
            skLineSegment(sketch, "E13.24.7", {"start": v(37.79, 14.96) * mm, "end": v(37.95, 14.57) * mm});
            skArc(sketch, "E13.24.8", {"start": v(36.34, 11.86) * mm, "mid": v(37.25, 12.72) * mm, "end": v(38.03, 13.7) * mm});
            skArc(sketch, "E13.24.9", {"start": v(36.1, 11.73) * mm, "mid": v(36.23, 11.78) * mm, "end": v(36.34, 11.86) * mm});
            skLineSegment(sketch, "E13.24.10", {"start": v(36.1, 11.73) * mm, "end": v(34.56, 11.16) * mm});
            skArc(sketch, "E13.24.11", {"start": v(34.56, 11.16) * mm, "mid": v(34.12, 10.77) * mm, "end": v(34.07, 10.18) * mm});
            skArc(sketch, "E13.25.0", {"start": v(28.26, 21.58) * mm, "mid": v(28.77, 21.28) * mm, "end": v(29.34, 21.4) * mm});
            skLineSegment(sketch, "E13.25.1", {"start": v(30.71, 22.32) * mm, "end": v(29.34, 21.4) * mm});
            skArc(sketch, "E13.25.2", {"start": v(30.96, 22.43) * mm, "mid": v(30.83, 22.39) * mm, "end": v(30.71, 22.32) * mm});
            skArc(sketch, "E13.25.3", {"start": v(30.96, 22.43) * mm, "mid": v(32.19, 22.65) * mm, "end": v(33.44, 22.72) * mm});
            skArc(sketch, "E13.25.4", {"start": v(33.85, 22.5) * mm, "mid": v(33.67, 22.66) * mm, "end": v(33.44, 22.72) * mm});
            skLineSegment(sketch, "E13.25.5", {"start": v(34.32, 21.77) * mm, "end": v(34.09, 22.14) * mm});
            skArc(sketch, "E13.25.6", {"start": v(34.35, 21.3) * mm, "mid": v(34.4, 21.54) * mm, "end": v(34.32, 21.77) * mm});
            skLineSegment(sketch, "E13.25.7", {"start": v(33.85, 22.5) * mm, "end": v(34.09, 22.14) * mm});
            skArc(sketch, "E13.25.8", {"start": v(33.08, 19.16) * mm, "mid": v(33.79, 20.2) * mm, "end": v(34.35, 21.3) * mm});
            skArc(sketch, "E13.25.9", {"start": v(32.88, 18.98) * mm, "mid": v(33, 19.06) * mm, "end": v(33.08, 19.16) * mm});
            skLineSegment(sketch, "E13.25.10", {"start": v(32.88, 18.98) * mm, "end": v(31.48, 18.1) * mm});
            skArc(sketch, "E13.25.11", {"start": v(31.48, 18.1) * mm, "mid": v(31.14, 17.62) * mm, "end": v(31.2, 17.04) * mm});
            skArc(sketch, "E13.26.0", {"start": v(23.16, 26.98) * mm, "mid": v(23.71, 26.8) * mm, "end": v(24.25, 27.03) * mm});
            skLineSegment(sketch, "E13.26.1", {"start": v(25.4, 28.22) * mm, "end": v(24.25, 27.03) * mm});
            skArc(sketch, "E13.26.2", {"start": v(25.62, 28.38) * mm, "mid": v(25.5, 28.3) * mm, "end": v(25.4, 28.22) * mm});
            skArc(sketch, "E13.26.3", {"start": v(25.62, 28.38) * mm, "mid": v(26.77, 28.85) * mm, "end": v(27.98, 29.17) * mm});
            skArc(sketch, "E13.26.4", {"start": v(28.43, 29.04) * mm, "mid": v(28.22, 29.16) * mm, "end": v(27.98, 29.17) * mm});
            skLineSegment(sketch, "E13.26.5", {"start": v(29.04, 28.43) * mm, "end": v(28.74, 28.74) * mm});
            skArc(sketch, "E13.26.6", {"start": v(29.17, 27.98) * mm, "mid": v(29.16, 28.22) * mm, "end": v(29.04, 28.43) * mm});
            skLineSegment(sketch, "E13.26.7", {"start": v(28.43, 29.04) * mm, "end": v(28.74, 28.74) * mm});
            skArc(sketch, "E13.26.8", {"start": v(28.38, 25.62) * mm, "mid": v(28.85, 26.77) * mm, "end": v(29.17, 27.98) * mm});
            skArc(sketch, "E13.26.9", {"start": v(28.22, 25.4) * mm, "mid": v(28.3, 25.5) * mm, "end": v(28.38, 25.62) * mm});
            skLineSegment(sketch, "E13.26.10", {"start": v(28.22, 25.4) * mm, "end": v(27.03, 24.25) * mm});
            skArc(sketch, "E13.26.11", {"start": v(27.03, 24.25) * mm, "mid": v(26.8, 23.71) * mm, "end": v(26.98, 23.16) * mm});
            skArc(sketch, "E13.27.0", {"start": v(17.04, 31.2) * mm, "mid": v(17.62, 31.14) * mm, "end": v(18.1, 31.48) * mm});
            skLineSegment(sketch, "E13.27.1", {"start": v(18.98, 32.88) * mm, "end": v(18.1, 31.48) * mm});
            skArc(sketch, "E13.27.2", {"start": v(19.16, 33.08) * mm, "mid": v(19.06, 33) * mm, "end": v(18.98, 32.88) * mm});
            skArc(sketch, "E13.27.3", {"start": v(19.16, 33.08) * mm, "mid": v(20.2, 33.79) * mm, "end": v(21.3, 34.35) * mm});
            skArc(sketch, "E13.27.4", {"start": v(21.77, 34.32) * mm, "mid": v(21.54, 34.4) * mm, "end": v(21.3, 34.35) * mm});
            skLineSegment(sketch, "E13.27.5", {"start": v(22.5, 33.85) * mm, "end": v(22.14, 34.09) * mm});
            skArc(sketch, "E13.27.6", {"start": v(22.72, 33.44) * mm, "mid": v(22.66, 33.67) * mm, "end": v(22.5, 33.85) * mm});
            skLineSegment(sketch, "E13.27.7", {"start": v(21.77, 34.32) * mm, "end": v(22.14, 34.09) * mm});
            skArc(sketch, "E13.27.8", {"start": v(22.43, 30.96) * mm, "mid": v(22.65, 32.19) * mm, "end": v(22.72, 33.44) * mm});
            skArc(sketch, "E13.27.9", {"start": v(22.32, 30.71) * mm, "mid": v(22.39, 30.83) * mm, "end": v(22.43, 30.96) * mm});
            skLineSegment(sketch, "E13.27.10", {"start": v(22.32, 30.71) * mm, "end": v(21.4, 29.34) * mm});
            skArc(sketch, "E13.27.11", {"start": v(21.4, 29.34) * mm, "mid": v(21.28, 28.77) * mm, "end": v(21.58, 28.26) * mm});
            skArc(sketch, "E13.28.0", {"start": v(10.18, 34.07) * mm, "mid": v(10.77, 34.12) * mm, "end": v(11.16, 34.56) * mm});
            skLineSegment(sketch, "E13.28.1", {"start": v(11.73, 36.1) * mm, "end": v(11.16, 34.56) * mm});
            skArc(sketch, "E13.28.2", {"start": v(11.86, 36.34) * mm, "mid": v(11.78, 36.23) * mm, "end": v(11.73, 36.1) * mm});
            skArc(sketch, "E13.28.3", {"start": v(11.86, 36.34) * mm, "mid": v(12.72, 37.25) * mm, "end": v(13.7, 38.03) * mm});
            skArc(sketch, "E13.28.4", {"start": v(14.16, 38.1) * mm, "mid": v(13.92, 38.12) * mm, "end": v(13.7, 38.03) * mm});
            skLineSegment(sketch, "E13.28.5", {"start": v(14.96, 37.79) * mm, "end": v(14.57, 37.95) * mm});
            skArc(sketch, "E13.28.6", {"start": v(15.27, 37.43) * mm, "mid": v(15.16, 37.64) * mm, "end": v(14.96, 37.79) * mm});
            skLineSegment(sketch, "E13.28.7", {"start": v(14.16, 38.1) * mm, "end": v(14.57, 37.95) * mm});
            skArc(sketch, "E13.28.8", {"start": v(15.5, 34.95) * mm, "mid": v(15.47, 36.2) * mm, "end": v(15.27, 37.43) * mm});
            skArc(sketch, "E13.28.9", {"start": v(15.45, 34.68) * mm, "mid": v(15.49, 34.81) * mm, "end": v(15.5, 34.95) * mm});
            skLineSegment(sketch, "E13.28.10", {"start": v(15.45, 34.68) * mm, "end": v(14.83, 33.14) * mm});
            skArc(sketch, "E13.28.11", {"start": v(14.83, 33.14) * mm, "mid": v(14.83, 32.56) * mm, "end": v(15.23, 32.13) * mm});
            skArc(sketch, "E13.29.0", {"start": v(2.88, 35.44) * mm, "mid": v(3.44, 35.61) * mm, "end": v(3.73, 36.12) * mm});
            skLineSegment(sketch, "E13.29.1", {"start": v(3.96, 37.76) * mm, "end": v(3.73, 36.12) * mm});
            skArc(sketch, "E13.29.2", {"start": v(4.05, 38.02) * mm, "mid": v(4, 37.9) * mm, "end": v(3.96, 37.76) * mm});
            skArc(sketch, "E13.29.3", {"start": v(4.05, 38.02) * mm, "mid": v(4.7, 39.08) * mm, "end": v(5.5, 40.05) * mm});
            skArc(sketch, "E13.29.4", {"start": v(5.93, 40.2) * mm, "mid": v(5.7, 40.18) * mm, "end": v(5.5, 40.05) * mm});
            skLineSegment(sketch, "E13.29.5", {"start": v(6.78, 40.07) * mm, "end": v(6.36, 40.15) * mm});
            skArc(sketch, "E13.29.6", {"start": v(7.15, 39.79) * mm, "mid": v(7, 39.97) * mm, "end": v(6.78, 40.07) * mm});
            skLineSegment(sketch, "E13.29.7", {"start": v(5.93, 40.2) * mm, "end": v(6.36, 40.15) * mm});
            skArc(sketch, "E13.29.8", {"start": v(7.9, 37.4) * mm, "mid": v(7.6, 38.62) * mm, "end": v(7.15, 39.79) * mm});
            skArc(sketch, "E13.29.9", {"start": v(7.9, 37.13) * mm, "mid": v(7.91, 37.27) * mm, "end": v(7.9, 37.4) * mm});
            skLineSegment(sketch, "E13.29.10", {"start": v(7.9, 37.13) * mm, "end": v(7.62, 35.5) * mm});
            skArc(sketch, "E13.29.11", {"start": v(7.62, 35.5) * mm, "mid": v(7.74, 34.93) * mm, "end": v(8.22, 34.6) * mm});
            skArc(sketch, "E14.trimOffspring", {"start": v(-11.79, 33.55) * mm, "mid": v(-12.74, 33.2) * mm, "end": v(-13.69, 32.82) * mm});
            skArc(sketch, "E15.trimOffspring", {"start": v(2.88, 35.44) * mm, "mid": v(1.86, 35.51) * mm, "end": v(0.84, 35.55) * mm});
            skArc(sketch, "E16.trimOffspring", {"start": v(-18.5, 30.37) * mm, "mid": v(-19.37, 29.82) * mm, "end": v(-20.21, 29.26) * mm});
            skArc(sketch, "E17.trimOffspring", {"start": v(-24.41, 25.85) * mm, "mid": v(-25.14, 25.14) * mm, "end": v(-25.85, 24.41) * mm});
            skArc(sketch, "E18.trimOffspring", {"start": v(-29.26, 20.21) * mm, "mid": v(-29.82, 19.37) * mm, "end": v(-30.37, 18.5) * mm});
            skArc(sketch, "E19.trimOffspring", {"start": v(-32.82, 13.69) * mm, "mid": v(-33.2, 12.74) * mm, "end": v(-33.55, 11.79) * mm});
            skArc(sketch, "E20.trimOffspring", {"start": v(10.18, 34.07) * mm, "mid": v(9.2, 34.35) * mm, "end": v(8.22, 34.6) * mm});
            skArc(sketch, "E21.trimOffspring", {"start": v(17.04, 31.2) * mm, "mid": v(16.14, 31.68) * mm, "end": v(15.23, 32.13) * mm});
            skArc(sketch, "E22.trimOffspring", {"start": v(23.16, 26.98) * mm, "mid": v(22.38, 27.64) * mm, "end": v(21.58, 28.26) * mm});
            skArc(sketch, "E23.trimOffspring", {"start": v(28.26, 21.58) * mm, "mid": v(27.64, 22.38) * mm, "end": v(26.98, 23.16) * mm});
            skArc(sketch, "E24.trimOffspring", {"start": v(32.13, 15.23) * mm, "mid": v(31.68, 16.14) * mm, "end": v(31.2, 17.04) * mm});
            skArc(sketch, "E25.trimOffspring", {"start": v(34.6, 8.22) * mm, "mid": v(34.35, 9.2) * mm, "end": v(34.07, 10.18) * mm});
            skArc(sketch, "E26.trimOffspring", {"start": v(-34.95, 6.57) * mm, "mid": v(-35.12, 5.56) * mm, "end": v(-35.27, 4.56) * mm});
            skArc(sketch, "E27.trimOffspring", {"start": v(35.55, 0.84) * mm, "mid": v(35.51, 1.86) * mm, "end": v(35.44, 2.88) * mm});
            skArc(sketch, "E28.trimOffspring", {"start": v(-35.55, -0.84) * mm, "mid": v(-35.51, -1.86) * mm, "end": v(-35.44, -2.88) * mm});
            skArc(sketch, "E29.trimOffspring", {"start": v(-32.13, -15.23) * mm, "mid": v(-31.68, -16.14) * mm, "end": v(-31.2, -17.04) * mm});
            skArc(sketch, "E30.trimOffspring", {"start": v(32.82, -13.69) * mm, "mid": v(33.2, -12.74) * mm, "end": v(33.55, -11.79) * mm});
            skArc(sketch, "E31.trimOffspring", {"start": v(-34.6, -8.22) * mm, "mid": v(-34.35, -9.2) * mm, "end": v(-34.07, -10.18) * mm});
            skArc(sketch, "E32.trimOffspring", {"start": v(-28.26, -21.58) * mm, "mid": v(-27.64, -22.38) * mm, "end": v(-26.98, -23.16) * mm});
            skArc(sketch, "E33.trimOffspring", {"start": v(-23.16, -26.98) * mm, "mid": v(-22.38, -27.64) * mm, "end": v(-21.58, -28.26) * mm});
            skArc(sketch, "E34.trimOffspring", {"start": v(34.95, -6.57) * mm, "mid": v(35.12, -5.56) * mm, "end": v(35.27, -4.56) * mm});
            skArc(sketch, "E35.trimOffspring", {"start": v(29.26, -20.21) * mm, "mid": v(29.82, -19.37) * mm, "end": v(30.37, -18.5) * mm});
            skArc(sketch, "E36.trimOffspring", {"start": v(24.41, -25.85) * mm, "mid": v(25.14, -25.14) * mm, "end": v(25.85, -24.41) * mm});
            skArc(sketch, "E37.trimOffspring", {"start": v(18.5, -30.37) * mm, "mid": v(19.37, -29.82) * mm, "end": v(20.21, -29.26) * mm});
            skArc(sketch, "E38.trimOffspring", {"start": v(11.79, -33.55) * mm, "mid": v(12.74, -33.2) * mm, "end": v(13.69, -32.82) * mm});
            skArc(sketch, "E39.trimOffspring", {"start": v(4.56, -35.27) * mm, "mid": v(5.56, -35.12) * mm, "end": v(6.57, -34.95) * mm});
            skArc(sketch, "E40.trimOffspring", {"start": v(-2.88, -35.44) * mm, "mid": v(-1.86, -35.51) * mm, "end": v(-0.84, -35.55) * mm});
            skArc(sketch, "E41.trimOffspring", {"start": v(-10.18, -34.07) * mm, "mid": v(-9.2, -34.35) * mm, "end": v(-8.22, -34.6) * mm});
            skArc(sketch, "E42.trimOffspring", {"start": v(-17.04, -31.2) * mm, "mid": v(-16.14, -31.68) * mm, "end": v(-15.23, -32.13) * mm});
            skSolve(sketch);
        }
        {
            var Q0;
            Q0 = qSketchRegion(id + "F0", true);
            extrude(context, id + "F1", {"entities" : qUnion([Q0]), "depth" : 114.3 * mm});
        }
        {
            var Q0;
            Q0=makeQuery(id+"F1.opExtrude","CAP_FACE",FACE,{"disambiguationData":[OSD([sQuery(id+"F0.wireOp",EDGE,"E0"),sQuery(id+"F0.wireOp",EDGE,"E1.trimOffspring"),sQuery(id+"F0.wireOp",EDGE,"E2"),sQuery(id+"F0.wireOp",EDGE,"E3"),sQuery(id+"F0.wireOp",EDGE,"E4.MirrorCS"),sQuery(id+"F0.wireOp",EDGE,"E5.MirrorCS"),sQuery(id+"F0.wireOp",EDGE,"E6.MirrorCS"),sQuery(id+"F0.wireOp",EDGE,"E7.filletArc"),sQuery(id+"F0.wireOp",EDGE,"E8.filletArc"),sQuery(id+"F0.wireOp",EDGE,"E9.filletArc"),sQuery(id+"F0.wireOp",EDGE,"E10.filletArc"),sQuery(id+"F0.wireOp",EDGE,"E11.filletArc"),sQuery(id+"F0.wireOp",EDGE,"E12.filletArc"),sQuery(id+"F0.wireOp",EDGE,"E13.1.0"),sQuery(id+"F0.wireOp",EDGE,"E13.1.1"),sQuery(id+"F0.wireOp",EDGE,"E13.1.2"),sQuery(id+"F0.wireOp",EDGE,"E13.1.3"),sQuery(id+"F0.wireOp",EDGE,"E13.1.4"),sQuery(id+"F0.wireOp",EDGE,"E13.1.5"),sQuery(id+"F0.wireOp",EDGE,"E13.1.6"),sQuery(id+"F0.wireOp",EDGE,"E13.1.7"),sQuery(id+"F0.wireOp",EDGE,"E13.1.8"),sQuery(id+"F0.wireOp",EDGE,"E13.1.9"),sQuery(id+"F0.wireOp",EDGE,"E13.1.10"),sQuery(id+"F0.wireOp",EDGE,"E13.1.11"),sQuery(id+"F0.wireOp",EDGE,"E13.2.0"),sQuery(id+"F0.wireOp",EDGE,"E13.2.1"),sQuery(id+"F0.wireOp",EDGE,"E13.2.2"),sQuery(id+"F0.wireOp",EDGE,"E13.2.3"),sQuery(id+"F0.wireOp",EDGE,"E13.2.4"),sQuery(id+"F0.wireOp",EDGE,"E13.2.5"),sQuery(id+"F0.wireOp",EDGE,"E13.2.6"),sQuery(id+"F0.wireOp",EDGE,"E13.2.7"),sQuery(id+"F0.wireOp",EDGE,"E13.2.8"),sQuery(id+"F0.wireOp",EDGE,"E13.2.9"),sQuery(id+"F0.wireOp",EDGE,"E13.2.10"),sQuery(id+"F0.wireOp",EDGE,"E13.2.11"),sQuery(id+"F0.wireOp",EDGE,"E13.3.0"),sQuery(id+"F0.wireOp",EDGE,"E13.3.1"),sQuery(id+"F0.wireOp",EDGE,"E13.3.2"),sQuery(id+"F0.wireOp",EDGE,"E13.3.3"),sQuery(id+"F0.wireOp",EDGE,"E13.3.4"),sQuery(id+"F0.wireOp",EDGE,"E13.3.5"),sQuery(id+"F0.wireOp",EDGE,"E13.3.6"),sQuery(id+"F0.wireOp",EDGE,"E13.3.7"),sQuery(id+"F0.wireOp",EDGE,"E13.3.8"),sQuery(id+"F0.wireOp",EDGE,"E13.3.9"),sQuery(id+"F0.wireOp",EDGE,"E13.3.10"),sQuery(id+"F0.wireOp",EDGE,"E13.3.11"),sQuery(id+"F0.wireOp",EDGE,"E13.4.0"),sQuery(id+"F0.wireOp",EDGE,"E13.4.1"),sQuery(id+"F0.wireOp",EDGE,"E13.4.2"),sQuery(id+"F0.wireOp",EDGE,"E13.4.3"),sQuery(id+"F0.wireOp",EDGE,"E13.4.4"),sQuery(id+"F0.wireOp",EDGE,"E13.4.5"),sQuery(id+"F0.wireOp",EDGE,"E13.4.6"),sQuery(id+"F0.wireOp",EDGE,"E13.4.7"),sQuery(id+"F0.wireOp",EDGE,"E13.4.8"),sQuery(id+"F0.wireOp",EDGE,"E13.4.9"),sQuery(id+"F0.wireOp",EDGE,"E13.4.10"),sQuery(id+"F0.wireOp",EDGE,"E13.4.11"),sQuery(id+"F0.wireOp",EDGE,"E13.5.0"),sQuery(id+"F0.wireOp",EDGE,"E13.5.1"),sQuery(id+"F0.wireOp",EDGE,"E13.5.2"),sQuery(id+"F0.wireOp",EDGE,"E13.5.3"),sQuery(id+"F0.wireOp",EDGE,"E13.5.4"),sQuery(id+"F0.wireOp",EDGE,"E13.5.5"),sQuery(id+"F0.wireOp",EDGE,"E13.5.6"),sQuery(id+"F0.wireOp",EDGE,"E13.5.7"),sQuery(id+"F0.wireOp",EDGE,"E13.5.8"),sQuery(id+"F0.wireOp",EDGE,"E13.5.9"),sQuery(id+"F0.wireOp",EDGE,"E13.5.10"),sQuery(id+"F0.wireOp",EDGE,"E13.5.11"),sQuery(id+"F0.wireOp",EDGE,"E13.6.0"),sQuery(id+"F0.wireOp",EDGE,"E13.6.1"),sQuery(id+"F0.wireOp",EDGE,"E13.6.2"),sQuery(id+"F0.wireOp",EDGE,"E13.6.3"),sQuery(id+"F0.wireOp",EDGE,"E13.6.4"),sQuery(id+"F0.wireOp",EDGE,"E13.6.5"),sQuery(id+"F0.wireOp",EDGE,"E13.6.6"),sQuery(id+"F0.wireOp",EDGE,"E13.6.7"),sQuery(id+"F0.wireOp",EDGE,"E13.6.8"),sQuery(id+"F0.wireOp",EDGE,"E13.6.9"),sQuery(id+"F0.wireOp",EDGE,"E13.6.10"),sQuery(id+"F0.wireOp",EDGE,"E13.6.11"),sQuery(id+"F0.wireOp",EDGE,"E13.7.0"),sQuery(id+"F0.wireOp",EDGE,"E13.7.1"),sQuery(id+"F0.wireOp",EDGE,"E13.7.2"),sQuery(id+"F0.wireOp",EDGE,"E13.7.3"),sQuery(id+"F0.wireOp",EDGE,"E13.7.4"),sQuery(id+"F0.wireOp",EDGE,"E13.7.5"),sQuery(id+"F0.wireOp",EDGE,"E13.7.6"),sQuery(id+"F0.wireOp",EDGE,"E13.7.7"),sQuery(id+"F0.wireOp",EDGE,"E13.7.8"),sQuery(id+"F0.wireOp",EDGE,"E13.7.9"),sQuery(id+"F0.wireOp",EDGE,"E13.7.10"),sQuery(id+"F0.wireOp",EDGE,"E13.7.11"),sQuery(id+"F0.wireOp",EDGE,"E13.8.0"),sQuery(id+"F0.wireOp",EDGE,"E13.8.1"),sQuery(id+"F0.wireOp",EDGE,"E13.8.2"),sQuery(id+"F0.wireOp",EDGE,"E13.8.3"),sQuery(id+"F0.wireOp",EDGE,"E13.8.4"),sQuery(id+"F0.wireOp",EDGE,"E13.8.5"),sQuery(id+"F0.wireOp",EDGE,"E13.8.6"),sQuery(id+"F0.wireOp",EDGE,"E13.8.7"),sQuery(id+"F0.wireOp",EDGE,"E13.8.8"),sQuery(id+"F0.wireOp",EDGE,"E13.8.9"),sQuery(id+"F0.wireOp",EDGE,"E13.8.10"),sQuery(id+"F0.wireOp",EDGE,"E13.8.11"),sQuery(id+"F0.wireOp",EDGE,"E13.9.0"),sQuery(id+"F0.wireOp",EDGE,"E13.9.1"),sQuery(id+"F0.wireOp",EDGE,"E13.9.2"),sQuery(id+"F0.wireOp",EDGE,"E13.9.3"),sQuery(id+"F0.wireOp",EDGE,"E13.9.4"),sQuery(id+"F0.wireOp",EDGE,"E13.9.5"),sQuery(id+"F0.wireOp",EDGE,"E13.9.6"),sQuery(id+"F0.wireOp",EDGE,"E13.9.7"),sQuery(id+"F0.wireOp",EDGE,"E13.9.8"),sQuery(id+"F0.wireOp",EDGE,"E13.9.9"),sQuery(id+"F0.wireOp",EDGE,"E13.9.10"),sQuery(id+"F0.wireOp",EDGE,"E13.9.11"),sQuery(id+"F0.wireOp",EDGE,"E13.10.0"),sQuery(id+"F0.wireOp",EDGE,"E13.10.1"),sQuery(id+"F0.wireOp",EDGE,"E13.10.2"),sQuery(id+"F0.wireOp",EDGE,"E13.10.3"),sQuery(id+"F0.wireOp",EDGE,"E13.10.4"),sQuery(id+"F0.wireOp",EDGE,"E13.10.5"),sQuery(id+"F0.wireOp",EDGE,"E13.10.6"),sQuery(id+"F0.wireOp",EDGE,"E13.10.7"),sQuery(id+"F0.wireOp",EDGE,"E13.10.8"),sQuery(id+"F0.wireOp",EDGE,"E13.10.9"),sQuery(id+"F0.wireOp",EDGE,"E13.10.10"),sQuery(id+"F0.wireOp",EDGE,"E13.10.11"),sQuery(id+"F0.wireOp",EDGE,"E13.11.0"),sQuery(id+"F0.wireOp",EDGE,"E13.11.1"),sQuery(id+"F0.wireOp",EDGE,"E13.11.2"),sQuery(id+"F0.wireOp",EDGE,"E13.11.3"),sQuery(id+"F0.wireOp",EDGE,"E13.11.4"),sQuery(id+"F0.wireOp",EDGE,"E13.11.5"),sQuery(id+"F0.wireOp",EDGE,"E13.11.6"),sQuery(id+"F0.wireOp",EDGE,"E13.11.7"),sQuery(id+"F0.wireOp",EDGE,"E13.11.8"),sQuery(id+"F0.wireOp",EDGE,"E13.11.9"),sQuery(id+"F0.wireOp",EDGE,"E13.11.10"),sQuery(id+"F0.wireOp",EDGE,"E13.11.11"),sQuery(id+"F0.wireOp",EDGE,"E13.12.0"),sQuery(id+"F0.wireOp",EDGE,"E13.12.1"),sQuery(id+"F0.wireOp",EDGE,"E13.12.2"),sQuery(id+"F0.wireOp",EDGE,"E13.12.3"),sQuery(id+"F0.wireOp",EDGE,"E13.12.4"),sQuery(id+"F0.wireOp",EDGE,"E13.12.5"),sQuery(id+"F0.wireOp",EDGE,"E13.12.6"),sQuery(id+"F0.wireOp",EDGE,"E13.12.7"),sQuery(id+"F0.wireOp",EDGE,"E13.12.8"),sQuery(id+"F0.wireOp",EDGE,"E13.12.9"),sQuery(id+"F0.wireOp",EDGE,"E13.12.10"),sQuery(id+"F0.wireOp",EDGE,"E13.12.11"),sQuery(id+"F0.wireOp",EDGE,"E13.13.0"),sQuery(id+"F0.wireOp",EDGE,"E13.13.1"),sQuery(id+"F0.wireOp",EDGE,"E13.13.2"),sQuery(id+"F0.wireOp",EDGE,"E13.13.3"),sQuery(id+"F0.wireOp",EDGE,"E13.13.4"),sQuery(id+"F0.wireOp",EDGE,"E13.13.5"),sQuery(id+"F0.wireOp",EDGE,"E13.13.6"),sQuery(id+"F0.wireOp",EDGE,"E13.13.7"),sQuery(id+"F0.wireOp",EDGE,"E13.13.8"),sQuery(id+"F0.wireOp",EDGE,"E13.13.9"),sQuery(id+"F0.wireOp",EDGE,"E13.13.10"),sQuery(id+"F0.wireOp",EDGE,"E13.13.11"),sQuery(id+"F0.wireOp",EDGE,"E13.14.0"),sQuery(id+"F0.wireOp",EDGE,"E13.14.1"),sQuery(id+"F0.wireOp",EDGE,"E13.14.2"),sQuery(id+"F0.wireOp",EDGE,"E13.14.3"),sQuery(id+"F0.wireOp",EDGE,"E13.14.4"),sQuery(id+"F0.wireOp",EDGE,"E13.14.5"),sQuery(id+"F0.wireOp",EDGE,"E13.14.6"),sQuery(id+"F0.wireOp",EDGE,"E13.14.7"),sQuery(id+"F0.wireOp",EDGE,"E13.14.8"),sQuery(id+"F0.wireOp",EDGE,"E13.14.9"),sQuery(id+"F0.wireOp",EDGE,"E13.14.10"),sQuery(id+"F0.wireOp",EDGE,"E13.14.11"),sQuery(id+"F0.wireOp",EDGE,"E13.15.0"),sQuery(id+"F0.wireOp",EDGE,"E13.15.1"),sQuery(id+"F0.wireOp",EDGE,"E13.15.2"),sQuery(id+"F0.wireOp",EDGE,"E13.15.3"),sQuery(id+"F0.wireOp",EDGE,"E13.15.4"),sQuery(id+"F0.wireOp",EDGE,"E13.15.5"),sQuery(id+"F0.wireOp",EDGE,"E13.15.6"),sQuery(id+"F0.wireOp",EDGE,"E13.15.7"),sQuery(id+"F0.wireOp",EDGE,"E13.15.8"),sQuery(id+"F0.wireOp",EDGE,"E13.15.9"),sQuery(id+"F0.wireOp",EDGE,"E13.15.10"),sQuery(id+"F0.wireOp",EDGE,"E13.15.11"),sQuery(id+"F0.wireOp",EDGE,"E13.16.0"),sQuery(id+"F0.wireOp",EDGE,"E13.16.1"),sQuery(id+"F0.wireOp",EDGE,"E13.16.2"),sQuery(id+"F0.wireOp",EDGE,"E13.16.3"),sQuery(id+"F0.wireOp",EDGE,"E13.16.4"),sQuery(id+"F0.wireOp",EDGE,"E13.16.5"),sQuery(id+"F0.wireOp",EDGE,"E13.16.6"),sQuery(id+"F0.wireOp",EDGE,"E13.16.7"),sQuery(id+"F0.wireOp",EDGE,"E13.16.8"),sQuery(id+"F0.wireOp",EDGE,"E13.16.9"),sQuery(id+"F0.wireOp",EDGE,"E13.16.10"),sQuery(id+"F0.wireOp",EDGE,"E13.16.11"),sQuery(id+"F0.wireOp",EDGE,"E13.17.0"),sQuery(id+"F0.wireOp",EDGE,"E13.17.1"),sQuery(id+"F0.wireOp",EDGE,"E13.17.2"),sQuery(id+"F0.wireOp",EDGE,"E13.17.3"),sQuery(id+"F0.wireOp",EDGE,"E13.17.4"),sQuery(id+"F0.wireOp",EDGE,"E13.17.5"),sQuery(id+"F0.wireOp",EDGE,"E13.17.6"),sQuery(id+"F0.wireOp",EDGE,"E13.17.7"),sQuery(id+"F0.wireOp",EDGE,"E13.17.8"),sQuery(id+"F0.wireOp",EDGE,"E13.17.9"),sQuery(id+"F0.wireOp",EDGE,"E13.17.10"),sQuery(id+"F0.wireOp",EDGE,"E13.17.11"),sQuery(id+"F0.wireOp",EDGE,"E13.18.0"),sQuery(id+"F0.wireOp",EDGE,"E13.18.1"),sQuery(id+"F0.wireOp",EDGE,"E13.18.2"),sQuery(id+"F0.wireOp",EDGE,"E13.18.3"),sQuery(id+"F0.wireOp",EDGE,"E13.18.4"),sQuery(id+"F0.wireOp",EDGE,"E13.18.5"),sQuery(id+"F0.wireOp",EDGE,"E13.18.6"),sQuery(id+"F0.wireOp",EDGE,"E13.18.7"),sQuery(id+"F0.wireOp",EDGE,"E13.18.8"),sQuery(id+"F0.wireOp",EDGE,"E13.18.9"),sQuery(id+"F0.wireOp",EDGE,"E13.18.10"),sQuery(id+"F0.wireOp",EDGE,"E13.18.11"),sQuery(id+"F0.wireOp",EDGE,"E13.19.0"),sQuery(id+"F0.wireOp",EDGE,"E13.19.1"),sQuery(id+"F0.wireOp",EDGE,"E13.19.2"),sQuery(id+"F0.wireOp",EDGE,"E13.19.3"),sQuery(id+"F0.wireOp",EDGE,"E13.19.4"),sQuery(id+"F0.wireOp",EDGE,"E13.19.5"),sQuery(id+"F0.wireOp",EDGE,"E13.19.6"),sQuery(id+"F0.wireOp",EDGE,"E13.19.7"),sQuery(id+"F0.wireOp",EDGE,"E13.19.8"),sQuery(id+"F0.wireOp",EDGE,"E13.19.9"),sQuery(id+"F0.wireOp",EDGE,"E13.19.10"),sQuery(id+"F0.wireOp",EDGE,"E13.19.11"),sQuery(id+"F0.wireOp",EDGE,"E13.20.0"),sQuery(id+"F0.wireOp",EDGE,"E13.20.1"),sQuery(id+"F0.wireOp",EDGE,"E13.20.2"),sQuery(id+"F0.wireOp",EDGE,"E13.20.3"),sQuery(id+"F0.wireOp",EDGE,"E13.20.4"),sQuery(id+"F0.wireOp",EDGE,"E13.20.5"),sQuery(id+"F0.wireOp",EDGE,"E13.20.6"),sQuery(id+"F0.wireOp",EDGE,"E13.20.7"),sQuery(id+"F0.wireOp",EDGE,"E13.20.8"),sQuery(id+"F0.wireOp",EDGE,"E13.20.9"),sQuery(id+"F0.wireOp",EDGE,"E13.20.10"),sQuery(id+"F0.wireOp",EDGE,"E13.20.11"),sQuery(id+"F0.wireOp",EDGE,"E13.21.0"),sQuery(id+"F0.wireOp",EDGE,"E13.21.1"),sQuery(id+"F0.wireOp",EDGE,"E13.21.2"),sQuery(id+"F0.wireOp",EDGE,"E13.21.3"),sQuery(id+"F0.wireOp",EDGE,"E13.21.4"),sQuery(id+"F0.wireOp",EDGE,"E13.21.5"),sQuery(id+"F0.wireOp",EDGE,"E13.21.6"),sQuery(id+"F0.wireOp",EDGE,"E13.21.7"),sQuery(id+"F0.wireOp",EDGE,"E13.21.8"),sQuery(id+"F0.wireOp",EDGE,"E13.21.9"),sQuery(id+"F0.wireOp",EDGE,"E13.21.10"),sQuery(id+"F0.wireOp",EDGE,"E13.21.11"),sQuery(id+"F0.wireOp",EDGE,"E13.22.0"),sQuery(id+"F0.wireOp",EDGE,"E13.22.1"),sQuery(id+"F0.wireOp",EDGE,"E13.22.2"),sQuery(id+"F0.wireOp",EDGE,"E13.22.3"),sQuery(id+"F0.wireOp",EDGE,"E13.22.4"),sQuery(id+"F0.wireOp",EDGE,"E13.22.5"),sQuery(id+"F0.wireOp",EDGE,"E13.22.6"),sQuery(id+"F0.wireOp",EDGE,"E13.22.7"),sQuery(id+"F0.wireOp",EDGE,"E13.22.8"),sQuery(id+"F0.wireOp",EDGE,"E13.22.9"),sQuery(id+"F0.wireOp",EDGE,"E13.22.10"),sQuery(id+"F0.wireOp",EDGE,"E13.22.11"),sQuery(id+"F0.wireOp",EDGE,"E13.23.0"),sQuery(id+"F0.wireOp",EDGE,"E13.23.1"),sQuery(id+"F0.wireOp",EDGE,"E13.23.2"),sQuery(id+"F0.wireOp",EDGE,"E13.23.3"),sQuery(id+"F0.wireOp",EDGE,"E13.23.4"),sQuery(id+"F0.wireOp",EDGE,"E13.23.5"),sQuery(id+"F0.wireOp",EDGE,"E13.23.6"),sQuery(id+"F0.wireOp",EDGE,"E13.23.7"),sQuery(id+"F0.wireOp",EDGE,"E13.23.8"),sQuery(id+"F0.wireOp",EDGE,"E13.23.9"),sQuery(id+"F0.wireOp",EDGE,"E13.23.10"),sQuery(id+"F0.wireOp",EDGE,"E13.23.11"),sQuery(id+"F0.wireOp",EDGE,"E13.24.0"),sQuery(id+"F0.wireOp",EDGE,"E13.24.1"),sQuery(id+"F0.wireOp",EDGE,"E13.24.2"),sQuery(id+"F0.wireOp",EDGE,"E13.24.3"),sQuery(id+"F0.wireOp",EDGE,"E13.24.4"),sQuery(id+"F0.wireOp",EDGE,"E13.24.5"),sQuery(id+"F0.wireOp",EDGE,"E13.24.6"),sQuery(id+"F0.wireOp",EDGE,"E13.24.7"),sQuery(id+"F0.wireOp",EDGE,"E13.24.8"),sQuery(id+"F0.wireOp",EDGE,"E13.24.9"),sQuery(id+"F0.wireOp",EDGE,"E13.24.10"),sQuery(id+"F0.wireOp",EDGE,"E13.24.11"),sQuery(id+"F0.wireOp",EDGE,"E13.25.0"),sQuery(id+"F0.wireOp",EDGE,"E13.25.1"),sQuery(id+"F0.wireOp",EDGE,"E13.25.2"),sQuery(id+"F0.wireOp",EDGE,"E13.25.3"),sQuery(id+"F0.wireOp",EDGE,"E13.25.4"),sQuery(id+"F0.wireOp",EDGE,"E13.25.5"),sQuery(id+"F0.wireOp",EDGE,"E13.25.6"),sQuery(id+"F0.wireOp",EDGE,"E13.25.7"),sQuery(id+"F0.wireOp",EDGE,"E13.25.8"),sQuery(id+"F0.wireOp",EDGE,"E13.25.9"),sQuery(id+"F0.wireOp",EDGE,"E13.25.10"),sQuery(id+"F0.wireOp",EDGE,"E13.25.11"),sQuery(id+"F0.wireOp",EDGE,"E13.26.0"),sQuery(id+"F0.wireOp",EDGE,"E13.26.1"),sQuery(id+"F0.wireOp",EDGE,"E13.26.2"),sQuery(id+"F0.wireOp",EDGE,"E13.26.3"),sQuery(id+"F0.wireOp",EDGE,"E13.26.4"),sQuery(id+"F0.wireOp",EDGE,"E13.26.5"),sQuery(id+"F0.wireOp",EDGE,"E13.26.6"),sQuery(id+"F0.wireOp",EDGE,"E13.26.7"),sQuery(id+"F0.wireOp",EDGE,"E13.26.8"),sQuery(id+"F0.wireOp",EDGE,"E13.26.9"),sQuery(id+"F0.wireOp",EDGE,"E13.26.10"),sQuery(id+"F0.wireOp",EDGE,"E13.26.11"),sQuery(id+"F0.wireOp",EDGE,"E13.27.0"),sQuery(id+"F0.wireOp",EDGE,"E13.27.1"),sQuery(id+"F0.wireOp",EDGE,"E13.27.2"),sQuery(id+"F0.wireOp",EDGE,"E13.27.3"),sQuery(id+"F0.wireOp",EDGE,"E13.27.4"),sQuery(id+"F0.wireOp",EDGE,"E13.27.5"),sQuery(id+"F0.wireOp",EDGE,"E13.27.6"),sQuery(id+"F0.wireOp",EDGE,"E13.27.7"),sQuery(id+"F0.wireOp",EDGE,"E13.27.8"),sQuery(id+"F0.wireOp",EDGE,"E13.27.9"),sQuery(id+"F0.wireOp",EDGE,"E13.27.10"),sQuery(id+"F0.wireOp",EDGE,"E13.27.11"),sQuery(id+"F0.wireOp",EDGE,"E13.28.0"),sQuery(id+"F0.wireOp",EDGE,"E13.28.1"),sQuery(id+"F0.wireOp",EDGE,"E13.28.2"),sQuery(id+"F0.wireOp",EDGE,"E13.28.3"),sQuery(id+"F0.wireOp",EDGE,"E13.28.4"),sQuery(id+"F0.wireOp",EDGE,"E13.28.5"),sQuery(id+"F0.wireOp",EDGE,"E13.28.6"),sQuery(id+"F0.wireOp",EDGE,"E13.28.7"),sQuery(id+"F0.wireOp",EDGE,"E13.28.8"),sQuery(id+"F0.wireOp",EDGE,"E13.28.9"),sQuery(id+"F0.wireOp",EDGE,"E13.28.10"),sQuery(id+"F0.wireOp",EDGE,"E13.28.11"),sQuery(id+"F0.wireOp",EDGE,"E13.29.0"),sQuery(id+"F0.wireOp",EDGE,"E13.29.1"),sQuery(id+"F0.wireOp",EDGE,"E13.29.2"),sQuery(id+"F0.wireOp",EDGE,"E13.29.3"),sQuery(id+"F0.wireOp",EDGE,"E13.29.4"),sQuery(id+"F0.wireOp",EDGE,"E13.29.5"),sQuery(id+"F0.wireOp",EDGE,"E13.29.6"),sQuery(id+"F0.wireOp",EDGE,"E13.29.7"),sQuery(id+"F0.wireOp",EDGE,"E13.29.8"),sQuery(id+"F0.wireOp",EDGE,"E13.29.9"),sQuery(id+"F0.wireOp",EDGE,"E13.29.10"),sQuery(id+"F0.wireOp",EDGE,"E13.29.11"),sQuery(id+"F0.wireOp",EDGE,"E14.trimOffspring"),sQuery(id+"F0.wireOp",EDGE,"E15.trimOffspring"),sQuery(id+"F0.wireOp",EDGE,"E16.trimOffspring"),sQuery(id+"F0.wireOp",EDGE,"E17.trimOffspring"),sQuery(id+"F0.wireOp",EDGE,"E18.trimOffspring"),sQuery(id+"F0.wireOp",EDGE,"E19.trimOffspring"),sQuery(id+"F0.wireOp",EDGE,"E20.trimOffspring"),sQuery(id+"F0.wireOp",EDGE,"E21.trimOffspring"),sQuery(id+"F0.wireOp",EDGE,"E22.trimOffspring"),sQuery(id+"F0.wireOp",EDGE,"E23.trimOffspring"),sQuery(id+"F0.wireOp",EDGE,"E24.trimOffspring"),sQuery(id+"F0.wireOp",EDGE,"E25.trimOffspring"),sQuery(id+"F0.wireOp",EDGE,"E26.trimOffspring"),sQuery(id+"F0.wireOp",EDGE,"E27.trimOffspring"),sQuery(id+"F0.wireOp",EDGE,"E28.trimOffspring"),sQuery(id+"F0.wireOp",EDGE,"E29.trimOffspring"),sQuery(id+"F0.wireOp",EDGE,"E30.trimOffspring"),sQuery(id+"F0.wireOp",EDGE,"E31.trimOffspring"),sQuery(id+"F0.wireOp",EDGE,"E32.trimOffspring"),sQuery(id+"F0.wireOp",EDGE,"E33.trimOffspring"),sQuery(id+"F0.wireOp",EDGE,"E34.trimOffspring"),sQuery(id+"F0.wireOp",EDGE,"E35.trimOffspring"),sQuery(id+"F0.wireOp",EDGE,"E36.trimOffspring"),sQuery(id+"F0.wireOp",EDGE,"E37.trimOffspring"),sQuery(id+"F0.wireOp",EDGE,"E38.trimOffspring"),sQuery(id+"F0.wireOp",EDGE,"E39.trimOffspring"),sQuery(id+"F0.wireOp",EDGE,"E40.trimOffspring"),sQuery(id+"F0.wireOp",EDGE,"E41.trimOffspring"),sQuery(id+"F0.wireOp",EDGE,"E42.trimOffspring")])],"isStart":false});
            var sketch = newSketch(context, id + "F2", { "sketchPlane" : qUnion([Q0])});
            skCircle(sketch, "E43", {"center": v(0, 0) * mm, "radius": 12.7 * mm});
            skCircle(sketch, "E44", {"center": v(0, 0) * mm, "radius": 6.35 * mm});
            skSolve(sketch);
        }
        {
            var Q0;
            Q0=makeQuery(id+"F2.imprint","IMPRINT",FACE,{"disambiguationData":[TD([[makeQuery(id+"F2.imprint","IMPRINT",EDGE,{"derivedFrom":sQuery(id+"F2.wireOp",EDGE,"E44")}),1.0]])]});
            extrude(context, id + "F3", {"entities" : qUnion([Q0]), "operationType" : NewBodyOperationType.REMOVE, "endBound" : BoundingType.THROUGH_ALL, "oppositeDirection" : true, "depth" : 12.7 * mm});
        }
        {
            var Q0;
            Q0=makeQuery(id+"F1.opExtrude","CAP_FACE",FACE,{"disambiguationData":[OSD([sQuery(id+"F0.wireOp",EDGE,"E0"),sQuery(id+"F0.wireOp",EDGE,"E1.trimOffspring"),sQuery(id+"F0.wireOp",EDGE,"E2"),sQuery(id+"F0.wireOp",EDGE,"E3"),sQuery(id+"F0.wireOp",EDGE,"E4.MirrorCS"),sQuery(id+"F0.wireOp",EDGE,"E5.MirrorCS"),sQuery(id+"F0.wireOp",EDGE,"E6.MirrorCS"),sQuery(id+"F0.wireOp",EDGE,"E7.filletArc"),sQuery(id+"F0.wireOp",EDGE,"E8.filletArc"),sQuery(id+"F0.wireOp",EDGE,"E9.filletArc"),sQuery(id+"F0.wireOp",EDGE,"E10.filletArc"),sQuery(id+"F0.wireOp",EDGE,"E11.filletArc"),sQuery(id+"F0.wireOp",EDGE,"E12.filletArc"),sQuery(id+"F0.wireOp",EDGE,"E13.1.0"),sQuery(id+"F0.wireOp",EDGE,"E13.1.1"),sQuery(id+"F0.wireOp",EDGE,"E13.1.2"),sQuery(id+"F0.wireOp",EDGE,"E13.1.3"),sQuery(id+"F0.wireOp",EDGE,"E13.1.4"),sQuery(id+"F0.wireOp",EDGE,"E13.1.5"),sQuery(id+"F0.wireOp",EDGE,"E13.1.6"),sQuery(id+"F0.wireOp",EDGE,"E13.1.7"),sQuery(id+"F0.wireOp",EDGE,"E13.1.8"),sQuery(id+"F0.wireOp",EDGE,"E13.1.9"),sQuery(id+"F0.wireOp",EDGE,"E13.1.10"),sQuery(id+"F0.wireOp",EDGE,"E13.1.11"),sQuery(id+"F0.wireOp",EDGE,"E13.2.0"),sQuery(id+"F0.wireOp",EDGE,"E13.2.1"),sQuery(id+"F0.wireOp",EDGE,"E13.2.2"),sQuery(id+"F0.wireOp",EDGE,"E13.2.3"),sQuery(id+"F0.wireOp",EDGE,"E13.2.4"),sQuery(id+"F0.wireOp",EDGE,"E13.2.5"),sQuery(id+"F0.wireOp",EDGE,"E13.2.6"),sQuery(id+"F0.wireOp",EDGE,"E13.2.7"),sQuery(id+"F0.wireOp",EDGE,"E13.2.8"),sQuery(id+"F0.wireOp",EDGE,"E13.2.9"),sQuery(id+"F0.wireOp",EDGE,"E13.2.10"),sQuery(id+"F0.wireOp",EDGE,"E13.2.11"),sQuery(id+"F0.wireOp",EDGE,"E13.3.0"),sQuery(id+"F0.wireOp",EDGE,"E13.3.1"),sQuery(id+"F0.wireOp",EDGE,"E13.3.2"),sQuery(id+"F0.wireOp",EDGE,"E13.3.3"),sQuery(id+"F0.wireOp",EDGE,"E13.3.4"),sQuery(id+"F0.wireOp",EDGE,"E13.3.5"),sQuery(id+"F0.wireOp",EDGE,"E13.3.6"),sQuery(id+"F0.wireOp",EDGE,"E13.3.7"),sQuery(id+"F0.wireOp",EDGE,"E13.3.8"),sQuery(id+"F0.wireOp",EDGE,"E13.3.9"),sQuery(id+"F0.wireOp",EDGE,"E13.3.10"),sQuery(id+"F0.wireOp",EDGE,"E13.3.11"),sQuery(id+"F0.wireOp",EDGE,"E13.4.0"),sQuery(id+"F0.wireOp",EDGE,"E13.4.1"),sQuery(id+"F0.wireOp",EDGE,"E13.4.2"),sQuery(id+"F0.wireOp",EDGE,"E13.4.3"),sQuery(id+"F0.wireOp",EDGE,"E13.4.4"),sQuery(id+"F0.wireOp",EDGE,"E13.4.5"),sQuery(id+"F0.wireOp",EDGE,"E13.4.6"),sQuery(id+"F0.wireOp",EDGE,"E13.4.7"),sQuery(id+"F0.wireOp",EDGE,"E13.4.8"),sQuery(id+"F0.wireOp",EDGE,"E13.4.9"),sQuery(id+"F0.wireOp",EDGE,"E13.4.10"),sQuery(id+"F0.wireOp",EDGE,"E13.4.11"),sQuery(id+"F0.wireOp",EDGE,"E13.5.0"),sQuery(id+"F0.wireOp",EDGE,"E13.5.1"),sQuery(id+"F0.wireOp",EDGE,"E13.5.2"),sQuery(id+"F0.wireOp",EDGE,"E13.5.3"),sQuery(id+"F0.wireOp",EDGE,"E13.5.4"),sQuery(id+"F0.wireOp",EDGE,"E13.5.5"),sQuery(id+"F0.wireOp",EDGE,"E13.5.6"),sQuery(id+"F0.wireOp",EDGE,"E13.5.7"),sQuery(id+"F0.wireOp",EDGE,"E13.5.8"),sQuery(id+"F0.wireOp",EDGE,"E13.5.9"),sQuery(id+"F0.wireOp",EDGE,"E13.5.10"),sQuery(id+"F0.wireOp",EDGE,"E13.5.11"),sQuery(id+"F0.wireOp",EDGE,"E13.6.0"),sQuery(id+"F0.wireOp",EDGE,"E13.6.1"),sQuery(id+"F0.wireOp",EDGE,"E13.6.2"),sQuery(id+"F0.wireOp",EDGE,"E13.6.3"),sQuery(id+"F0.wireOp",EDGE,"E13.6.4"),sQuery(id+"F0.wireOp",EDGE,"E13.6.5"),sQuery(id+"F0.wireOp",EDGE,"E13.6.6"),sQuery(id+"F0.wireOp",EDGE,"E13.6.7"),sQuery(id+"F0.wireOp",EDGE,"E13.6.8"),sQuery(id+"F0.wireOp",EDGE,"E13.6.9"),sQuery(id+"F0.wireOp",EDGE,"E13.6.10"),sQuery(id+"F0.wireOp",EDGE,"E13.6.11"),sQuery(id+"F0.wireOp",EDGE,"E13.7.0"),sQuery(id+"F0.wireOp",EDGE,"E13.7.1"),sQuery(id+"F0.wireOp",EDGE,"E13.7.2"),sQuery(id+"F0.wireOp",EDGE,"E13.7.3"),sQuery(id+"F0.wireOp",EDGE,"E13.7.4"),sQuery(id+"F0.wireOp",EDGE,"E13.7.5"),sQuery(id+"F0.wireOp",EDGE,"E13.7.6"),sQuery(id+"F0.wireOp",EDGE,"E13.7.7"),sQuery(id+"F0.wireOp",EDGE,"E13.7.8"),sQuery(id+"F0.wireOp",EDGE,"E13.7.9"),sQuery(id+"F0.wireOp",EDGE,"E13.7.10"),sQuery(id+"F0.wireOp",EDGE,"E13.7.11"),sQuery(id+"F0.wireOp",EDGE,"E13.8.0"),sQuery(id+"F0.wireOp",EDGE,"E13.8.1"),sQuery(id+"F0.wireOp",EDGE,"E13.8.2"),sQuery(id+"F0.wireOp",EDGE,"E13.8.3"),sQuery(id+"F0.wireOp",EDGE,"E13.8.4"),sQuery(id+"F0.wireOp",EDGE,"E13.8.5"),sQuery(id+"F0.wireOp",EDGE,"E13.8.6"),sQuery(id+"F0.wireOp",EDGE,"E13.8.7"),sQuery(id+"F0.wireOp",EDGE,"E13.8.8"),sQuery(id+"F0.wireOp",EDGE,"E13.8.9"),sQuery(id+"F0.wireOp",EDGE,"E13.8.10"),sQuery(id+"F0.wireOp",EDGE,"E13.8.11"),sQuery(id+"F0.wireOp",EDGE,"E13.9.0"),sQuery(id+"F0.wireOp",EDGE,"E13.9.1"),sQuery(id+"F0.wireOp",EDGE,"E13.9.2"),sQuery(id+"F0.wireOp",EDGE,"E13.9.3"),sQuery(id+"F0.wireOp",EDGE,"E13.9.4"),sQuery(id+"F0.wireOp",EDGE,"E13.9.5"),sQuery(id+"F0.wireOp",EDGE,"E13.9.6"),sQuery(id+"F0.wireOp",EDGE,"E13.9.7"),sQuery(id+"F0.wireOp",EDGE,"E13.9.8"),sQuery(id+"F0.wireOp",EDGE,"E13.9.9"),sQuery(id+"F0.wireOp",EDGE,"E13.9.10"),sQuery(id+"F0.wireOp",EDGE,"E13.9.11"),sQuery(id+"F0.wireOp",EDGE,"E13.10.0"),sQuery(id+"F0.wireOp",EDGE,"E13.10.1"),sQuery(id+"F0.wireOp",EDGE,"E13.10.2"),sQuery(id+"F0.wireOp",EDGE,"E13.10.3"),sQuery(id+"F0.wireOp",EDGE,"E13.10.4"),sQuery(id+"F0.wireOp",EDGE,"E13.10.5"),sQuery(id+"F0.wireOp",EDGE,"E13.10.6"),sQuery(id+"F0.wireOp",EDGE,"E13.10.7"),sQuery(id+"F0.wireOp",EDGE,"E13.10.8"),sQuery(id+"F0.wireOp",EDGE,"E13.10.9"),sQuery(id+"F0.wireOp",EDGE,"E13.10.10"),sQuery(id+"F0.wireOp",EDGE,"E13.10.11"),sQuery(id+"F0.wireOp",EDGE,"E13.11.0"),sQuery(id+"F0.wireOp",EDGE,"E13.11.1"),sQuery(id+"F0.wireOp",EDGE,"E13.11.2"),sQuery(id+"F0.wireOp",EDGE,"E13.11.3"),sQuery(id+"F0.wireOp",EDGE,"E13.11.4"),sQuery(id+"F0.wireOp",EDGE,"E13.11.5"),sQuery(id+"F0.wireOp",EDGE,"E13.11.6"),sQuery(id+"F0.wireOp",EDGE,"E13.11.7"),sQuery(id+"F0.wireOp",EDGE,"E13.11.8"),sQuery(id+"F0.wireOp",EDGE,"E13.11.9"),sQuery(id+"F0.wireOp",EDGE,"E13.11.10"),sQuery(id+"F0.wireOp",EDGE,"E13.11.11"),sQuery(id+"F0.wireOp",EDGE,"E13.12.0"),sQuery(id+"F0.wireOp",EDGE,"E13.12.1"),sQuery(id+"F0.wireOp",EDGE,"E13.12.2"),sQuery(id+"F0.wireOp",EDGE,"E13.12.3"),sQuery(id+"F0.wireOp",EDGE,"E13.12.4"),sQuery(id+"F0.wireOp",EDGE,"E13.12.5"),sQuery(id+"F0.wireOp",EDGE,"E13.12.6"),sQuery(id+"F0.wireOp",EDGE,"E13.12.7"),sQuery(id+"F0.wireOp",EDGE,"E13.12.8"),sQuery(id+"F0.wireOp",EDGE,"E13.12.9"),sQuery(id+"F0.wireOp",EDGE,"E13.12.10"),sQuery(id+"F0.wireOp",EDGE,"E13.12.11"),sQuery(id+"F0.wireOp",EDGE,"E13.13.0"),sQuery(id+"F0.wireOp",EDGE,"E13.13.1"),sQuery(id+"F0.wireOp",EDGE,"E13.13.2"),sQuery(id+"F0.wireOp",EDGE,"E13.13.3"),sQuery(id+"F0.wireOp",EDGE,"E13.13.4"),sQuery(id+"F0.wireOp",EDGE,"E13.13.5"),sQuery(id+"F0.wireOp",EDGE,"E13.13.6"),sQuery(id+"F0.wireOp",EDGE,"E13.13.7"),sQuery(id+"F0.wireOp",EDGE,"E13.13.8"),sQuery(id+"F0.wireOp",EDGE,"E13.13.9"),sQuery(id+"F0.wireOp",EDGE,"E13.13.10"),sQuery(id+"F0.wireOp",EDGE,"E13.13.11"),sQuery(id+"F0.wireOp",EDGE,"E13.14.0"),sQuery(id+"F0.wireOp",EDGE,"E13.14.1"),sQuery(id+"F0.wireOp",EDGE,"E13.14.2"),sQuery(id+"F0.wireOp",EDGE,"E13.14.3"),sQuery(id+"F0.wireOp",EDGE,"E13.14.4"),sQuery(id+"F0.wireOp",EDGE,"E13.14.5"),sQuery(id+"F0.wireOp",EDGE,"E13.14.6"),sQuery(id+"F0.wireOp",EDGE,"E13.14.7"),sQuery(id+"F0.wireOp",EDGE,"E13.14.8"),sQuery(id+"F0.wireOp",EDGE,"E13.14.9"),sQuery(id+"F0.wireOp",EDGE,"E13.14.10"),sQuery(id+"F0.wireOp",EDGE,"E13.14.11"),sQuery(id+"F0.wireOp",EDGE,"E13.15.0"),sQuery(id+"F0.wireOp",EDGE,"E13.15.1"),sQuery(id+"F0.wireOp",EDGE,"E13.15.2"),sQuery(id+"F0.wireOp",EDGE,"E13.15.3"),sQuery(id+"F0.wireOp",EDGE,"E13.15.4"),sQuery(id+"F0.wireOp",EDGE,"E13.15.5"),sQuery(id+"F0.wireOp",EDGE,"E13.15.6"),sQuery(id+"F0.wireOp",EDGE,"E13.15.7"),sQuery(id+"F0.wireOp",EDGE,"E13.15.8"),sQuery(id+"F0.wireOp",EDGE,"E13.15.9"),sQuery(id+"F0.wireOp",EDGE,"E13.15.10"),sQuery(id+"F0.wireOp",EDGE,"E13.15.11"),sQuery(id+"F0.wireOp",EDGE,"E13.16.0"),sQuery(id+"F0.wireOp",EDGE,"E13.16.1"),sQuery(id+"F0.wireOp",EDGE,"E13.16.2"),sQuery(id+"F0.wireOp",EDGE,"E13.16.3"),sQuery(id+"F0.wireOp",EDGE,"E13.16.4"),sQuery(id+"F0.wireOp",EDGE,"E13.16.5"),sQuery(id+"F0.wireOp",EDGE,"E13.16.6"),sQuery(id+"F0.wireOp",EDGE,"E13.16.7"),sQuery(id+"F0.wireOp",EDGE,"E13.16.8"),sQuery(id+"F0.wireOp",EDGE,"E13.16.9"),sQuery(id+"F0.wireOp",EDGE,"E13.16.10"),sQuery(id+"F0.wireOp",EDGE,"E13.16.11"),sQuery(id+"F0.wireOp",EDGE,"E13.17.0"),sQuery(id+"F0.wireOp",EDGE,"E13.17.1"),sQuery(id+"F0.wireOp",EDGE,"E13.17.2"),sQuery(id+"F0.wireOp",EDGE,"E13.17.3"),sQuery(id+"F0.wireOp",EDGE,"E13.17.4"),sQuery(id+"F0.wireOp",EDGE,"E13.17.5"),sQuery(id+"F0.wireOp",EDGE,"E13.17.6"),sQuery(id+"F0.wireOp",EDGE,"E13.17.7"),sQuery(id+"F0.wireOp",EDGE,"E13.17.8"),sQuery(id+"F0.wireOp",EDGE,"E13.17.9"),sQuery(id+"F0.wireOp",EDGE,"E13.17.10"),sQuery(id+"F0.wireOp",EDGE,"E13.17.11"),sQuery(id+"F0.wireOp",EDGE,"E13.18.0"),sQuery(id+"F0.wireOp",EDGE,"E13.18.1"),sQuery(id+"F0.wireOp",EDGE,"E13.18.2"),sQuery(id+"F0.wireOp",EDGE,"E13.18.3"),sQuery(id+"F0.wireOp",EDGE,"E13.18.4"),sQuery(id+"F0.wireOp",EDGE,"E13.18.5"),sQuery(id+"F0.wireOp",EDGE,"E13.18.6"),sQuery(id+"F0.wireOp",EDGE,"E13.18.7"),sQuery(id+"F0.wireOp",EDGE,"E13.18.8"),sQuery(id+"F0.wireOp",EDGE,"E13.18.9"),sQuery(id+"F0.wireOp",EDGE,"E13.18.10"),sQuery(id+"F0.wireOp",EDGE,"E13.18.11"),sQuery(id+"F0.wireOp",EDGE,"E13.19.0"),sQuery(id+"F0.wireOp",EDGE,"E13.19.1"),sQuery(id+"F0.wireOp",EDGE,"E13.19.2"),sQuery(id+"F0.wireOp",EDGE,"E13.19.3"),sQuery(id+"F0.wireOp",EDGE,"E13.19.4"),sQuery(id+"F0.wireOp",EDGE,"E13.19.5"),sQuery(id+"F0.wireOp",EDGE,"E13.19.6"),sQuery(id+"F0.wireOp",EDGE,"E13.19.7"),sQuery(id+"F0.wireOp",EDGE,"E13.19.8"),sQuery(id+"F0.wireOp",EDGE,"E13.19.9"),sQuery(id+"F0.wireOp",EDGE,"E13.19.10"),sQuery(id+"F0.wireOp",EDGE,"E13.19.11"),sQuery(id+"F0.wireOp",EDGE,"E13.20.0"),sQuery(id+"F0.wireOp",EDGE,"E13.20.1"),sQuery(id+"F0.wireOp",EDGE,"E13.20.2"),sQuery(id+"F0.wireOp",EDGE,"E13.20.3"),sQuery(id+"F0.wireOp",EDGE,"E13.20.4"),sQuery(id+"F0.wireOp",EDGE,"E13.20.5"),sQuery(id+"F0.wireOp",EDGE,"E13.20.6"),sQuery(id+"F0.wireOp",EDGE,"E13.20.7"),sQuery(id+"F0.wireOp",EDGE,"E13.20.8"),sQuery(id+"F0.wireOp",EDGE,"E13.20.9"),sQuery(id+"F0.wireOp",EDGE,"E13.20.10"),sQuery(id+"F0.wireOp",EDGE,"E13.20.11"),sQuery(id+"F0.wireOp",EDGE,"E13.21.0"),sQuery(id+"F0.wireOp",EDGE,"E13.21.1"),sQuery(id+"F0.wireOp",EDGE,"E13.21.2"),sQuery(id+"F0.wireOp",EDGE,"E13.21.3"),sQuery(id+"F0.wireOp",EDGE,"E13.21.4"),sQuery(id+"F0.wireOp",EDGE,"E13.21.5"),sQuery(id+"F0.wireOp",EDGE,"E13.21.6"),sQuery(id+"F0.wireOp",EDGE,"E13.21.7"),sQuery(id+"F0.wireOp",EDGE,"E13.21.8"),sQuery(id+"F0.wireOp",EDGE,"E13.21.9"),sQuery(id+"F0.wireOp",EDGE,"E13.21.10"),sQuery(id+"F0.wireOp",EDGE,"E13.21.11"),sQuery(id+"F0.wireOp",EDGE,"E13.22.0"),sQuery(id+"F0.wireOp",EDGE,"E13.22.1"),sQuery(id+"F0.wireOp",EDGE,"E13.22.2"),sQuery(id+"F0.wireOp",EDGE,"E13.22.3"),sQuery(id+"F0.wireOp",EDGE,"E13.22.4"),sQuery(id+"F0.wireOp",EDGE,"E13.22.5"),sQuery(id+"F0.wireOp",EDGE,"E13.22.6"),sQuery(id+"F0.wireOp",EDGE,"E13.22.7"),sQuery(id+"F0.wireOp",EDGE,"E13.22.8"),sQuery(id+"F0.wireOp",EDGE,"E13.22.9"),sQuery(id+"F0.wireOp",EDGE,"E13.22.10"),sQuery(id+"F0.wireOp",EDGE,"E13.22.11"),sQuery(id+"F0.wireOp",EDGE,"E13.23.0"),sQuery(id+"F0.wireOp",EDGE,"E13.23.1"),sQuery(id+"F0.wireOp",EDGE,"E13.23.2"),sQuery(id+"F0.wireOp",EDGE,"E13.23.3"),sQuery(id+"F0.wireOp",EDGE,"E13.23.4"),sQuery(id+"F0.wireOp",EDGE,"E13.23.5"),sQuery(id+"F0.wireOp",EDGE,"E13.23.6"),sQuery(id+"F0.wireOp",EDGE,"E13.23.7"),sQuery(id+"F0.wireOp",EDGE,"E13.23.8"),sQuery(id+"F0.wireOp",EDGE,"E13.23.9"),sQuery(id+"F0.wireOp",EDGE,"E13.23.10"),sQuery(id+"F0.wireOp",EDGE,"E13.23.11"),sQuery(id+"F0.wireOp",EDGE,"E13.24.0"),sQuery(id+"F0.wireOp",EDGE,"E13.24.1"),sQuery(id+"F0.wireOp",EDGE,"E13.24.2"),sQuery(id+"F0.wireOp",EDGE,"E13.24.3"),sQuery(id+"F0.wireOp",EDGE,"E13.24.4"),sQuery(id+"F0.wireOp",EDGE,"E13.24.5"),sQuery(id+"F0.wireOp",EDGE,"E13.24.6"),sQuery(id+"F0.wireOp",EDGE,"E13.24.7"),sQuery(id+"F0.wireOp",EDGE,"E13.24.8"),sQuery(id+"F0.wireOp",EDGE,"E13.24.9"),sQuery(id+"F0.wireOp",EDGE,"E13.24.10"),sQuery(id+"F0.wireOp",EDGE,"E13.24.11"),sQuery(id+"F0.wireOp",EDGE,"E13.25.0"),sQuery(id+"F0.wireOp",EDGE,"E13.25.1"),sQuery(id+"F0.wireOp",EDGE,"E13.25.2"),sQuery(id+"F0.wireOp",EDGE,"E13.25.3"),sQuery(id+"F0.wireOp",EDGE,"E13.25.4"),sQuery(id+"F0.wireOp",EDGE,"E13.25.5"),sQuery(id+"F0.wireOp",EDGE,"E13.25.6"),sQuery(id+"F0.wireOp",EDGE,"E13.25.7"),sQuery(id+"F0.wireOp",EDGE,"E13.25.8"),sQuery(id+"F0.wireOp",EDGE,"E13.25.9"),sQuery(id+"F0.wireOp",EDGE,"E13.25.10"),sQuery(id+"F0.wireOp",EDGE,"E13.25.11"),sQuery(id+"F0.wireOp",EDGE,"E13.26.0"),sQuery(id+"F0.wireOp",EDGE,"E13.26.1"),sQuery(id+"F0.wireOp",EDGE,"E13.26.2"),sQuery(id+"F0.wireOp",EDGE,"E13.26.3"),sQuery(id+"F0.wireOp",EDGE,"E13.26.4"),sQuery(id+"F0.wireOp",EDGE,"E13.26.5"),sQuery(id+"F0.wireOp",EDGE,"E13.26.6"),sQuery(id+"F0.wireOp",EDGE,"E13.26.7"),sQuery(id+"F0.wireOp",EDGE,"E13.26.8"),sQuery(id+"F0.wireOp",EDGE,"E13.26.9"),sQuery(id+"F0.wireOp",EDGE,"E13.26.10"),sQuery(id+"F0.wireOp",EDGE,"E13.26.11"),sQuery(id+"F0.wireOp",EDGE,"E13.27.0"),sQuery(id+"F0.wireOp",EDGE,"E13.27.1"),sQuery(id+"F0.wireOp",EDGE,"E13.27.2"),sQuery(id+"F0.wireOp",EDGE,"E13.27.3"),sQuery(id+"F0.wireOp",EDGE,"E13.27.4"),sQuery(id+"F0.wireOp",EDGE,"E13.27.5"),sQuery(id+"F0.wireOp",EDGE,"E13.27.6"),sQuery(id+"F0.wireOp",EDGE,"E13.27.7"),sQuery(id+"F0.wireOp",EDGE,"E13.27.8"),sQuery(id+"F0.wireOp",EDGE,"E13.27.9"),sQuery(id+"F0.wireOp",EDGE,"E13.27.10"),sQuery(id+"F0.wireOp",EDGE,"E13.27.11"),sQuery(id+"F0.wireOp",EDGE,"E13.28.0"),sQuery(id+"F0.wireOp",EDGE,"E13.28.1"),sQuery(id+"F0.wireOp",EDGE,"E13.28.2"),sQuery(id+"F0.wireOp",EDGE,"E13.28.3"),sQuery(id+"F0.wireOp",EDGE,"E13.28.4"),sQuery(id+"F0.wireOp",EDGE,"E13.28.5"),sQuery(id+"F0.wireOp",EDGE,"E13.28.6"),sQuery(id+"F0.wireOp",EDGE,"E13.28.7"),sQuery(id+"F0.wireOp",EDGE,"E13.28.8"),sQuery(id+"F0.wireOp",EDGE,"E13.28.9"),sQuery(id+"F0.wireOp",EDGE,"E13.28.10"),sQuery(id+"F0.wireOp",EDGE,"E13.28.11"),sQuery(id+"F0.wireOp",EDGE,"E13.29.0"),sQuery(id+"F0.wireOp",EDGE,"E13.29.1"),sQuery(id+"F0.wireOp",EDGE,"E13.29.2"),sQuery(id+"F0.wireOp",EDGE,"E13.29.3"),sQuery(id+"F0.wireOp",EDGE,"E13.29.4"),sQuery(id+"F0.wireOp",EDGE,"E13.29.5"),sQuery(id+"F0.wireOp",EDGE,"E13.29.6"),sQuery(id+"F0.wireOp",EDGE,"E13.29.7"),sQuery(id+"F0.wireOp",EDGE,"E13.29.8"),sQuery(id+"F0.wireOp",EDGE,"E13.29.9"),sQuery(id+"F0.wireOp",EDGE,"E13.29.10"),sQuery(id+"F0.wireOp",EDGE,"E13.29.11"),sQuery(id+"F0.wireOp",EDGE,"E14.trimOffspring"),sQuery(id+"F0.wireOp",EDGE,"E15.trimOffspring"),sQuery(id+"F0.wireOp",EDGE,"E16.trimOffspring"),sQuery(id+"F0.wireOp",EDGE,"E17.trimOffspring"),sQuery(id+"F0.wireOp",EDGE,"E18.trimOffspring"),sQuery(id+"F0.wireOp",EDGE,"E19.trimOffspring"),sQuery(id+"F0.wireOp",EDGE,"E20.trimOffspring"),sQuery(id+"F0.wireOp",EDGE,"E21.trimOffspring"),sQuery(id+"F0.wireOp",EDGE,"E22.trimOffspring"),sQuery(id+"F0.wireOp",EDGE,"E23.trimOffspring"),sQuery(id+"F0.wireOp",EDGE,"E24.trimOffspring"),sQuery(id+"F0.wireOp",EDGE,"E25.trimOffspring"),sQuery(id+"F0.wireOp",EDGE,"E26.trimOffspring"),sQuery(id+"F0.wireOp",EDGE,"E27.trimOffspring"),sQuery(id+"F0.wireOp",EDGE,"E28.trimOffspring"),sQuery(id+"F0.wireOp",EDGE,"E29.trimOffspring"),sQuery(id+"F0.wireOp",EDGE,"E30.trimOffspring"),sQuery(id+"F0.wireOp",EDGE,"E31.trimOffspring"),sQuery(id+"F0.wireOp",EDGE,"E32.trimOffspring"),sQuery(id+"F0.wireOp",EDGE,"E33.trimOffspring"),sQuery(id+"F0.wireOp",EDGE,"E34.trimOffspring"),sQuery(id+"F0.wireOp",EDGE,"E35.trimOffspring"),sQuery(id+"F0.wireOp",EDGE,"E36.trimOffspring"),sQuery(id+"F0.wireOp",EDGE,"E37.trimOffspring"),sQuery(id+"F0.wireOp",EDGE,"E38.trimOffspring"),sQuery(id+"F0.wireOp",EDGE,"E39.trimOffspring"),sQuery(id+"F0.wireOp",EDGE,"E40.trimOffspring"),sQuery(id+"F0.wireOp",EDGE,"E41.trimOffspring"),sQuery(id+"F0.wireOp",EDGE,"E42.trimOffspring")])],"isStart":false});
            var sketch = newSketch(context, id + "F4", { "sketchPlane" : qUnion([Q0])});
            skCircle(sketch, "E45", {"center": v(0, 0) * mm, "radius": 12.7 * mm});
            skSolve(sketch);
        }
        {
            var Q0;
            Q0=makeQuery(id+"F4.imprint","IMPRINT",FACE,{"disambiguationData":[TD([[makeQuery(id+"F4.imprint","IMPRINT",EDGE,{"derivedFrom":sQuery(id+"F4.wireOp",EDGE,"E45")}),1.0]])]});
            extrude(context, id + "F5", {"entities" : qUnion([Q0]), "operationType" : NewBodyOperationType.ADD, "depth" : 12.7 * mm});
        }
    });
